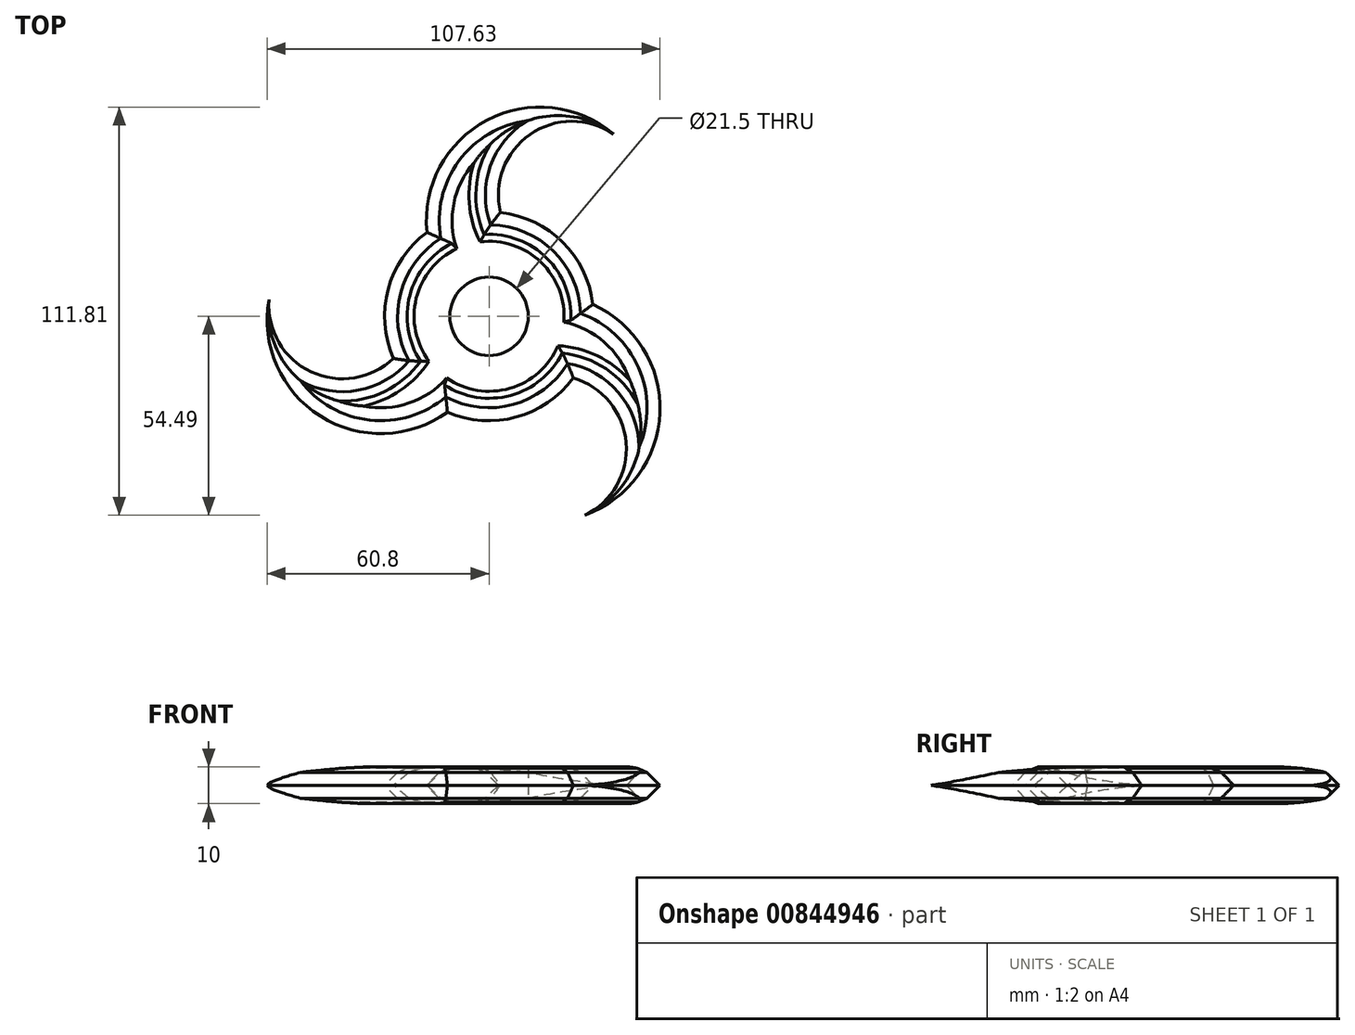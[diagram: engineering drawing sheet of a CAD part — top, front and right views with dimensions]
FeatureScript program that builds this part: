
annotation { "Feature Type Name" : "Feature", "Feature Type Description" : "" }
export const myFeature = defineFeature(function(context is Context, id is Id, definition is map)
    precondition{}
    {
        {
            var Q0;
            Q0=qCreatedBy(makeId("Top.planeOp"),FACE);
            var sketch = newSketch(context, id + "F0", { "sketchPlane" : qUnion([Q0])});
            skCircle(sketch, "E0", {"center": v(0, 0) * mm, "radius": 10.75 * mm});
            skCircle(sketch, "E1", {"center": v(0, 0) * mm, "radius": 28.6 * mm});
            skArc(sketch, "E2", {"start": v(34.08, 49.96) * mm, "mid": v(11.21, 49.81) * mm, "end": v(3.12, 28.43) * mm});
            skArc(sketch, "E3", {"start": v(34.08, 49.96) * mm, "mid": v(-0.57, 53.71) * mm, "end": v(-17.02, 22.99) * mm});
            skArc(sketch, "E4.1.0", {"start": v(-60.3, 4.53) * mm, "mid": v(-46.23, -27.35) * mm, "end": v(-11.4, -26.23) * mm});
            skArc(sketch, "E4.1.1", {"start": v(-60.3, 4.53) * mm, "mid": v(-48.75, -15.2) * mm, "end": v(-26.18, -11.52) * mm});
            skArc(sketch, "E4.2.0", {"start": v(26.23, -54.49) * mm, "mid": v(46.8, -26.36) * mm, "end": v(28.42, 3.24) * mm});
            skArc(sketch, "E4.2.1", {"start": v(26.23, -54.49) * mm, "mid": v(37.53, -34.62) * mm, "end": v(23.06, -16.92) * mm});
            skSolve(sketch);
        }
        {
            var Q0;
            Q0=makeQuery(id+"F0.imprint","IMPRINT",FACE,{"disambiguationData":[TD([[makeQuery(id+"F0.imprint","IMPRINT",EDGE,{"derivedFrom":sQuery(id+"F0.wireOp",EDGE,"E0")}),-1.0]])]});
            extrude(context, id + "F1", {"entities" : qUnion([Q0]), "depth" : 10 * mm, "offsetDistance" : 25 * mm});
        }
        {
            var Q0;
            {var subQ0=sQuery(id+"F0.wireOp",EDGE,"E2");Q0=makeQuery(id+"F0.imprint","IMPRINT",FACE,{"disambiguationData":[TD([[makeQuery(id+"F0.imprint","IMPRINT",EDGE,{"derivedFrom":subQ0}),-1.0]])]});}
            var Q1;
            {var subQ0=sQuery(id+"F0.wireOp",EDGE,"E4.1.0");Q1=makeQuery(id+"F0.imprint","IMPRINT",FACE,{"disambiguationData":[TD([[makeQuery(id+"F0.imprint","IMPRINT",EDGE,{"derivedFrom":subQ0}),1.0]])]});}
            var Q2;
            {var subQ0=sQuery(id+"F0.wireOp",EDGE,"E4.2.0");Q2=makeQuery(id+"F0.imprint","IMPRINT",FACE,{"disambiguationData":[TD([[makeQuery(id+"F0.imprint","IMPRINT",EDGE,{"derivedFrom":subQ0}),1.0]])]});}
            var Q3;
            {var subQ0=sQuery(id+"F0.wireOp",EDGE,"E4.3.0");Q3=makeQuery(id+"F0.imprint","IMPRINT",FACE,{"disambiguationData":[TD([[makeQuery(id+"F0.imprint","IMPRINT",EDGE,{"derivedFrom":subQ0}),1.0]])]});}
            var Q4;
            {var subQ0=sQuery(id+"F0.wireOp",EDGE,"E4.4.0");Q4=makeQuery(id+"F0.imprint","IMPRINT",FACE,{"disambiguationData":[TD([[makeQuery(id+"F0.imprint","IMPRINT",EDGE,{"derivedFrom":subQ0}),1.0]])]});}
            extrude(context, id + "F2", {"entities" : qUnion([Q0, Q1, Q2, Q3, Q4]), "operationType" : NewBodyOperationType.ADD, "depth" : 10 * mm, "offsetDistance" : 25 * mm});
        }
        {
            var Q0;
            Q0=makeQuery(id+"F2.opExtrude","CAP_EDGE",EDGE,{"disambiguationData":[OSD([sQuery(id+"F0.wireOp",EDGE,"E4.1.1")])],"isStart":false});
            var Q1;
            Q1=makeQuery(id+"F2.opExtrude","CAP_EDGE",EDGE,{"disambiguationData":[OSD([sQuery(id+"F0.wireOp",EDGE,"E2")])],"isStart":false});
            var Q2;
            Q2=makeQuery(id+"F2.opExtrude","CAP_EDGE",EDGE,{"disambiguationData":[OSD([sQuery(id+"F0.wireOp",EDGE,"E4.4.1")])],"isStart":false});
            var Q3;
            Q3=makeQuery(id+"F2.opExtrude","CAP_EDGE",EDGE,{"disambiguationData":[OSD([sQuery(id+"F0.wireOp",EDGE,"E4.3.1")])],"isStart":false});
            var Q4;
            Q4=makeQuery(id+"F2.opExtrude","CAP_EDGE",EDGE,{"disambiguationData":[OSD([sQuery(id+"F0.wireOp",EDGE,"E4.2.1")])],"isStart":false});
            var Q5;
            Q5=makeQuery(id+"F2.opExtrude","CAP_EDGE",EDGE,{"disambiguationData":[OSD([sQuery(id+"F0.wireOp",EDGE,"E3")])],"isStart":false});
            var Q6;
            Q6=makeQuery(id+"F2.opExtrude","CAP_EDGE",EDGE,{"disambiguationData":[OSD([sQuery(id+"F0.wireOp",EDGE,"E4.4.0")])],"isStart":false});
            var Q7;
            Q7=makeQuery(id+"F2.opExtrude","CAP_EDGE",EDGE,{"disambiguationData":[OSD([sQuery(id+"F0.wireOp",EDGE,"E4.3.0")])],"isStart":false});
            var Q8;
            Q8=makeQuery(id+"F2.opExtrude","CAP_EDGE",EDGE,{"disambiguationData":[OSD([sQuery(id+"F0.wireOp",EDGE,"E4.2.0")])],"isStart":false});
            var Q9;
            Q9=makeQuery(id+"F2.opExtrude","CAP_EDGE",EDGE,{"disambiguationData":[OSD([sQuery(id+"F0.wireOp",EDGE,"E4.1.0")])],"isStart":false});
            chamfer(context, id + "F3", {"entities" : qUnion([Q0, Q1, Q2, Q3, Q4, Q5, Q6, Q7, Q8, Q9]), "width" : 5 * mm, "tangentPropagation" : true});
        }
        {
            var Q0;
            {var subQ0=sQuery(id+"F0.wireOp",EDGE,"E3");var subQ1=sQuery(id+"F0.wireOp",EDGE,"E1");Q0=makeQuery(id+"F2.boolean.opBoolean","SPLIT",EDGE,{"disambiguationData":[TD([makeQuery(id+"F2.opExtrude","SWEPT_FACE",FACE,{"disambiguationData":[OSD([subQ0])]})])],"derivedFrom":makeQuery(id+"F1.opExtrude","CAP_EDGE",EDGE,{"disambiguationData":[OSD([subQ1])],"isStart":false})});}
            var Q1;
            {var subQ0=sQuery(id+"F0.wireOp",EDGE,"E2");var subQ1=sQuery(id+"F0.wireOp",EDGE,"E1");Q1=makeQuery(id+"F2.boolean.opBoolean","SPLIT",EDGE,{"disambiguationData":[TD([makeQuery(id+"F2.opExtrude","SWEPT_FACE",FACE,{"disambiguationData":[OSD([subQ0])]})])],"derivedFrom":makeQuery(id+"F1.opExtrude","CAP_EDGE",EDGE,{"disambiguationData":[OSD([subQ1])],"isStart":false})});}
            var Q2;
            {var subQ0=sQuery(id+"F0.wireOp",EDGE,"E1");var subQ2=sQuery(id+"F0.wireOp",EDGE,"E4.3.0");Q2=makeQuery(id+"F2.boolean.opBoolean","SPLIT",EDGE,{"disambiguationData":[TD([makeQuery(id+"F2.opExtrude","SWEPT_FACE",FACE,{"disambiguationData":[OSD([subQ2])]})])],"derivedFrom":makeQuery(id+"F1.opExtrude","CAP_EDGE",EDGE,{"disambiguationData":[OSD([subQ0])],"isStart":false})});}
            var Q3;
            {var subQ0=sQuery(id+"F0.wireOp",EDGE,"E1");var subQ1=sQuery(id+"F0.wireOp",EDGE,"E4.2.0");Q3=makeQuery(id+"F2.boolean.opBoolean","SPLIT",EDGE,{"disambiguationData":[TD([makeQuery(id+"F2.opExtrude","SWEPT_FACE",FACE,{"disambiguationData":[OSD([subQ1])]})])],"derivedFrom":makeQuery(id+"F1.opExtrude","CAP_EDGE",EDGE,{"disambiguationData":[OSD([subQ0])],"isStart":false})});}
            var Q4;
            {var subQ0=sQuery(id+"F0.wireOp",EDGE,"E1");var subQ2=sQuery(id+"F0.wireOp",EDGE,"E4.1.0");Q4=makeQuery(id+"F2.boolean.opBoolean","SPLIT",EDGE,{"disambiguationData":[TD([makeQuery(id+"F2.opExtrude","SWEPT_FACE",FACE,{"disambiguationData":[OSD([subQ2])]})])],"derivedFrom":makeQuery(id+"F1.opExtrude","CAP_EDGE",EDGE,{"disambiguationData":[OSD([subQ0])],"isStart":false})});}
            chamfer(context, id + "F4", {"entities" : qUnion([Q0, Q1, Q2, Q3, Q4]), "width" : 5 * mm, "tangentPropagation" : true});
        }
        {
            var Q0;
            {var subQ0=sQuery(id+"F0.wireOp",EDGE,"E2");var subQ1=sQuery(id+"F0.wireOp",EDGE,"E1");Q0=makeQuery(id+"F2.boolean.opBoolean","SPLIT",EDGE,{"disambiguationData":[TD([makeQuery(id+"F2.opExtrude","SWEPT_FACE",FACE,{"disambiguationData":[OSD([subQ0])]})])],"derivedFrom":makeQuery(id+"F1.opExtrude","CAP_EDGE",EDGE,{"disambiguationData":[OSD([subQ1])],"isStart":true})});}
            var Q1;
            Q1=makeQuery(id+"F2.opExtrude","CAP_EDGE",EDGE,{"disambiguationData":[OSD([sQuery(id+"F0.wireOp",EDGE,"E4.4.0")])],"isStart":true});
            var Q2;
            Q2=makeQuery(id+"F2.opExtrude","CAP_EDGE",EDGE,{"disambiguationData":[OSD([sQuery(id+"F0.wireOp",EDGE,"E4.4.1")])],"isStart":true});
            var Q3;
            {var subQ0=sQuery(id+"F0.wireOp",EDGE,"E1");var subQ2=sQuery(id+"F0.wireOp",EDGE,"E4.3.0");Q3=makeQuery(id+"F2.boolean.opBoolean","SPLIT",EDGE,{"disambiguationData":[TD([makeQuery(id+"F2.opExtrude","SWEPT_FACE",FACE,{"disambiguationData":[OSD([subQ2])]})])],"derivedFrom":makeQuery(id+"F1.opExtrude","CAP_EDGE",EDGE,{"disambiguationData":[OSD([subQ0])],"isStart":true})});}
            var Q4;
            Q4=makeQuery(id+"F2.opExtrude","CAP_EDGE",EDGE,{"disambiguationData":[OSD([sQuery(id+"F0.wireOp",EDGE,"E4.3.0")])],"isStart":true});
            var Q5;
            Q5=makeQuery(id+"F2.opExtrude","CAP_EDGE",EDGE,{"disambiguationData":[OSD([sQuery(id+"F0.wireOp",EDGE,"E4.3.1")])],"isStart":true});
            var Q6;
            Q6=makeQuery(id+"F2.opExtrude","CAP_EDGE",EDGE,{"disambiguationData":[OSD([sQuery(id+"F0.wireOp",EDGE,"E4.2.0")])],"isStart":true});
            var Q7;
            Q7=makeQuery(id+"F2.opExtrude","CAP_EDGE",EDGE,{"disambiguationData":[OSD([sQuery(id+"F0.wireOp",EDGE,"E4.2.1")])],"isStart":true});
            var Q8;
            Q8=makeQuery(id+"F2.opExtrude","CAP_EDGE",EDGE,{"disambiguationData":[OSD([sQuery(id+"F0.wireOp",EDGE,"E4.1.0")])],"isStart":true});
            var Q9;
            Q9=makeQuery(id+"F2.opExtrude","CAP_EDGE",EDGE,{"disambiguationData":[OSD([sQuery(id+"F0.wireOp",EDGE,"E4.1.1")])],"isStart":true});
            var Q10;
            Q10=makeQuery(id+"F2.opExtrude","CAP_EDGE",EDGE,{"disambiguationData":[OSD([sQuery(id+"F0.wireOp",EDGE,"E2")])],"isStart":true});
            var Q11;
            Q11=makeQuery(id+"F2.opExtrude","CAP_EDGE",EDGE,{"disambiguationData":[OSD([sQuery(id+"F0.wireOp",EDGE,"E3")])],"isStart":true});
            var Q12;
            {var subQ0=sQuery(id+"F0.wireOp",EDGE,"E3");var subQ1=sQuery(id+"F0.wireOp",EDGE,"E1");Q12=makeQuery(id+"F2.boolean.opBoolean","SPLIT",EDGE,{"disambiguationData":[TD([makeQuery(id+"F2.opExtrude","SWEPT_FACE",FACE,{"disambiguationData":[OSD([subQ0])]})])],"derivedFrom":makeQuery(id+"F1.opExtrude","CAP_EDGE",EDGE,{"disambiguationData":[OSD([subQ1])],"isStart":true})});}
            var Q13;
            {var subQ0=sQuery(id+"F0.wireOp",EDGE,"E1");var subQ2=sQuery(id+"F0.wireOp",EDGE,"E4.1.0");Q13=makeQuery(id+"F2.boolean.opBoolean","SPLIT",EDGE,{"disambiguationData":[TD([makeQuery(id+"F2.opExtrude","SWEPT_FACE",FACE,{"disambiguationData":[OSD([subQ2])]})])],"derivedFrom":makeQuery(id+"F1.opExtrude","CAP_EDGE",EDGE,{"disambiguationData":[OSD([subQ0])],"isStart":true})});}
            var Q14;
            {var subQ0=sQuery(id+"F0.wireOp",EDGE,"E1");var subQ1=sQuery(id+"F0.wireOp",EDGE,"E4.2.0");Q14=makeQuery(id+"F2.boolean.opBoolean","SPLIT",EDGE,{"disambiguationData":[TD([makeQuery(id+"F2.opExtrude","SWEPT_FACE",FACE,{"disambiguationData":[OSD([subQ1])]})])],"derivedFrom":makeQuery(id+"F1.opExtrude","CAP_EDGE",EDGE,{"disambiguationData":[OSD([subQ0])],"isStart":true})});}
            chamfer(context, id + "F5", {"entities" : qUnion([Q0, Q1, Q2, Q3, Q4, Q5, Q6, Q7, Q8, Q9, Q10, Q11, Q12, Q13, Q14]), "width" : 5 * mm, "tangentPropagation" : true});
        }
        {
            var Q0;
            {var subQ0=sQuery(id+"F0.wireOp",EDGE,"E1");var subQ1=sQuery(id+"F0.wireOp",EDGE,"E3");Q0=makeQuery(id+"F5.opChamfer","BLEND_EDGE",EDGE,{"blendedFrom":[makeQuery(id+"F2.opExtrude","CAP_EDGE",EDGE,{"disambiguationData":[OSD([subQ1])],"isStart":true}),makeQuery(id+"F2.boolean.opBoolean","MERGE",FACE,{"derivedFrom":[makeQuery(id+"F1.opExtrude","CAP_FACE",FACE,{"disambiguationData":[OSD([sQuery(id+"F0.wireOp",EDGE,"E0"),subQ0])],"isStart":true}),makeQuery(id+"F2.opExtrude","CAP_FACE",FACE,{"disambiguationData":[OSD([subQ0,sQuery(id+"F0.wireOp",EDGE,"E4.4.0"),sQuery(id+"F0.wireOp",EDGE,"E4.4.1")])],"isStart":true}),makeQuery(id+"F2.opExtrude","CAP_FACE",FACE,{"disambiguationData":[OSD([subQ0,sQuery(id+"F0.wireOp",EDGE,"E2"),subQ1])],"isStart":true}),makeQuery(id+"F2.opExtrude","CAP_FACE",FACE,{"disambiguationData":[OSD([subQ0,sQuery(id+"F0.wireOp",EDGE,"E4.1.0"),sQuery(id+"F0.wireOp",EDGE,"E4.1.1")])],"isStart":true}),makeQuery(id+"F2.opExtrude","CAP_FACE",FACE,{"disambiguationData":[OSD([subQ0,sQuery(id+"F0.wireOp",EDGE,"E4.2.0"),sQuery(id+"F0.wireOp",EDGE,"E4.2.1")])],"isStart":true}),makeQuery(id+"F2.opExtrude","CAP_FACE",FACE,{"disambiguationData":[OSD([subQ0,sQuery(id+"F0.wireOp",EDGE,"E4.3.0"),sQuery(id+"F0.wireOp",EDGE,"E4.3.1")])],"isStart":true})]})],"blendedInto":[makeQuery(id+"F2.boolean.opBoolean","MERGE",FACE,{"derivedFrom":[makeQuery(id+"F1.opExtrude","CAP_FACE",FACE,{"disambiguationData":[OSD([sQuery(id+"F0.wireOp",EDGE,"E0"),subQ0])],"isStart":true}),makeQuery(id+"F2.opExtrude","CAP_FACE",FACE,{"disambiguationData":[OSD([subQ0,sQuery(id+"F0.wireOp",EDGE,"E4.4.0"),sQuery(id+"F0.wireOp",EDGE,"E4.4.1")])],"isStart":true}),makeQuery(id+"F2.opExtrude","CAP_FACE",FACE,{"disambiguationData":[OSD([subQ0,sQuery(id+"F0.wireOp",EDGE,"E2"),subQ1])],"isStart":true}),makeQuery(id+"F2.opExtrude","CAP_FACE",FACE,{"disambiguationData":[OSD([subQ0,sQuery(id+"F0.wireOp",EDGE,"E4.1.0"),sQuery(id+"F0.wireOp",EDGE,"E4.1.1")])],"isStart":true}),makeQuery(id+"F2.opExtrude","CAP_FACE",FACE,{"disambiguationData":[OSD([subQ0,sQuery(id+"F0.wireOp",EDGE,"E4.2.0"),sQuery(id+"F0.wireOp",EDGE,"E4.2.1")])],"isStart":true}),makeQuery(id+"F2.opExtrude","CAP_FACE",FACE,{"disambiguationData":[OSD([subQ0,sQuery(id+"F0.wireOp",EDGE,"E4.3.0"),sQuery(id+"F0.wireOp",EDGE,"E4.3.1")])],"isStart":true})]})]});}
            var Q1;
            {var subQ0=sQuery(id+"F0.wireOp",EDGE,"E1");var subQ1=sQuery(id+"F0.wireOp",EDGE,"E2");Q1=makeQuery(id+"F5.opChamfer","BLEND_EDGE",EDGE,{"blendedFrom":[makeQuery(id+"F2.opExtrude","CAP_EDGE",EDGE,{"disambiguationData":[OSD([subQ1])],"isStart":true}),makeQuery(id+"F2.boolean.opBoolean","MERGE",FACE,{"derivedFrom":[makeQuery(id+"F1.opExtrude","CAP_FACE",FACE,{"disambiguationData":[OSD([sQuery(id+"F0.wireOp",EDGE,"E0"),subQ0])],"isStart":true}),makeQuery(id+"F2.opExtrude","CAP_FACE",FACE,{"disambiguationData":[OSD([subQ0,sQuery(id+"F0.wireOp",EDGE,"E4.4.0"),sQuery(id+"F0.wireOp",EDGE,"E4.4.1")])],"isStart":true}),makeQuery(id+"F2.opExtrude","CAP_FACE",FACE,{"disambiguationData":[OSD([subQ0,subQ1,sQuery(id+"F0.wireOp",EDGE,"E3")])],"isStart":true}),makeQuery(id+"F2.opExtrude","CAP_FACE",FACE,{"disambiguationData":[OSD([subQ0,sQuery(id+"F0.wireOp",EDGE,"E4.1.0"),sQuery(id+"F0.wireOp",EDGE,"E4.1.1")])],"isStart":true}),makeQuery(id+"F2.opExtrude","CAP_FACE",FACE,{"disambiguationData":[OSD([subQ0,sQuery(id+"F0.wireOp",EDGE,"E4.2.0"),sQuery(id+"F0.wireOp",EDGE,"E4.2.1")])],"isStart":true}),makeQuery(id+"F2.opExtrude","CAP_FACE",FACE,{"disambiguationData":[OSD([subQ0,sQuery(id+"F0.wireOp",EDGE,"E4.3.0"),sQuery(id+"F0.wireOp",EDGE,"E4.3.1")])],"isStart":true})]})],"blendedInto":[makeQuery(id+"F2.boolean.opBoolean","MERGE",FACE,{"derivedFrom":[makeQuery(id+"F1.opExtrude","CAP_FACE",FACE,{"disambiguationData":[OSD([sQuery(id+"F0.wireOp",EDGE,"E0"),subQ0])],"isStart":true}),makeQuery(id+"F2.opExtrude","CAP_FACE",FACE,{"disambiguationData":[OSD([subQ0,sQuery(id+"F0.wireOp",EDGE,"E4.4.0"),sQuery(id+"F0.wireOp",EDGE,"E4.4.1")])],"isStart":true}),makeQuery(id+"F2.opExtrude","CAP_FACE",FACE,{"disambiguationData":[OSD([subQ0,subQ1,sQuery(id+"F0.wireOp",EDGE,"E3")])],"isStart":true}),makeQuery(id+"F2.opExtrude","CAP_FACE",FACE,{"disambiguationData":[OSD([subQ0,sQuery(id+"F0.wireOp",EDGE,"E4.1.0"),sQuery(id+"F0.wireOp",EDGE,"E4.1.1")])],"isStart":true}),makeQuery(id+"F2.opExtrude","CAP_FACE",FACE,{"disambiguationData":[OSD([subQ0,sQuery(id+"F0.wireOp",EDGE,"E4.2.0"),sQuery(id+"F0.wireOp",EDGE,"E4.2.1")])],"isStart":true}),makeQuery(id+"F2.opExtrude","CAP_FACE",FACE,{"disambiguationData":[OSD([subQ0,sQuery(id+"F0.wireOp",EDGE,"E4.3.0"),sQuery(id+"F0.wireOp",EDGE,"E4.3.1")])],"isStart":true})]})]});}
            var Q2;
            {var subQ0=sQuery(id+"F0.wireOp",EDGE,"E1");var subQ1=sQuery(id+"F0.wireOp",EDGE,"E4.1.1");Q2=makeQuery(id+"F5.opChamfer","BLEND_EDGE",EDGE,{"blendedFrom":[makeQuery(id+"F2.opExtrude","CAP_EDGE",EDGE,{"disambiguationData":[OSD([subQ1])],"isStart":true}),makeQuery(id+"F2.boolean.opBoolean","MERGE",FACE,{"derivedFrom":[makeQuery(id+"F1.opExtrude","CAP_FACE",FACE,{"disambiguationData":[OSD([sQuery(id+"F0.wireOp",EDGE,"E0"),subQ0])],"isStart":true}),makeQuery(id+"F2.opExtrude","CAP_FACE",FACE,{"disambiguationData":[OSD([subQ0,sQuery(id+"F0.wireOp",EDGE,"E4.4.0"),sQuery(id+"F0.wireOp",EDGE,"E4.4.1")])],"isStart":true}),makeQuery(id+"F2.opExtrude","CAP_FACE",FACE,{"disambiguationData":[OSD([subQ0,sQuery(id+"F0.wireOp",EDGE,"E2"),sQuery(id+"F0.wireOp",EDGE,"E3")])],"isStart":true}),makeQuery(id+"F2.opExtrude","CAP_FACE",FACE,{"disambiguationData":[OSD([subQ0,sQuery(id+"F0.wireOp",EDGE,"E4.1.0"),subQ1])],"isStart":true}),makeQuery(id+"F2.opExtrude","CAP_FACE",FACE,{"disambiguationData":[OSD([subQ0,sQuery(id+"F0.wireOp",EDGE,"E4.2.0"),sQuery(id+"F0.wireOp",EDGE,"E4.2.1")])],"isStart":true}),makeQuery(id+"F2.opExtrude","CAP_FACE",FACE,{"disambiguationData":[OSD([subQ0,sQuery(id+"F0.wireOp",EDGE,"E4.3.0"),sQuery(id+"F0.wireOp",EDGE,"E4.3.1")])],"isStart":true})]})],"blendedInto":[makeQuery(id+"F2.boolean.opBoolean","MERGE",FACE,{"derivedFrom":[makeQuery(id+"F1.opExtrude","CAP_FACE",FACE,{"disambiguationData":[OSD([sQuery(id+"F0.wireOp",EDGE,"E0"),subQ0])],"isStart":true}),makeQuery(id+"F2.opExtrude","CAP_FACE",FACE,{"disambiguationData":[OSD([subQ0,sQuery(id+"F0.wireOp",EDGE,"E4.4.0"),sQuery(id+"F0.wireOp",EDGE,"E4.4.1")])],"isStart":true}),makeQuery(id+"F2.opExtrude","CAP_FACE",FACE,{"disambiguationData":[OSD([subQ0,sQuery(id+"F0.wireOp",EDGE,"E2"),sQuery(id+"F0.wireOp",EDGE,"E3")])],"isStart":true}),makeQuery(id+"F2.opExtrude","CAP_FACE",FACE,{"disambiguationData":[OSD([subQ0,sQuery(id+"F0.wireOp",EDGE,"E4.1.0"),subQ1])],"isStart":true}),makeQuery(id+"F2.opExtrude","CAP_FACE",FACE,{"disambiguationData":[OSD([subQ0,sQuery(id+"F0.wireOp",EDGE,"E4.2.0"),sQuery(id+"F0.wireOp",EDGE,"E4.2.1")])],"isStart":true}),makeQuery(id+"F2.opExtrude","CAP_FACE",FACE,{"disambiguationData":[OSD([subQ0,sQuery(id+"F0.wireOp",EDGE,"E4.3.0"),sQuery(id+"F0.wireOp",EDGE,"E4.3.1")])],"isStart":true})]})]});}
            var Q3;
            {var subQ0=sQuery(id+"F0.wireOp",EDGE,"E1");var subQ1=sQuery(id+"F0.wireOp",EDGE,"E4.1.0");Q3=makeQuery(id+"F5.opChamfer","BLEND_EDGE",EDGE,{"blendedFrom":[makeQuery(id+"F2.opExtrude","CAP_EDGE",EDGE,{"disambiguationData":[OSD([subQ1])],"isStart":true}),makeQuery(id+"F2.boolean.opBoolean","MERGE",FACE,{"derivedFrom":[makeQuery(id+"F1.opExtrude","CAP_FACE",FACE,{"disambiguationData":[OSD([sQuery(id+"F0.wireOp",EDGE,"E0"),subQ0])],"isStart":true}),makeQuery(id+"F2.opExtrude","CAP_FACE",FACE,{"disambiguationData":[OSD([subQ0,sQuery(id+"F0.wireOp",EDGE,"E4.4.0"),sQuery(id+"F0.wireOp",EDGE,"E4.4.1")])],"isStart":true}),makeQuery(id+"F2.opExtrude","CAP_FACE",FACE,{"disambiguationData":[OSD([subQ0,sQuery(id+"F0.wireOp",EDGE,"E2"),sQuery(id+"F0.wireOp",EDGE,"E3")])],"isStart":true}),makeQuery(id+"F2.opExtrude","CAP_FACE",FACE,{"disambiguationData":[OSD([subQ0,subQ1,sQuery(id+"F0.wireOp",EDGE,"E4.1.1")])],"isStart":true}),makeQuery(id+"F2.opExtrude","CAP_FACE",FACE,{"disambiguationData":[OSD([subQ0,sQuery(id+"F0.wireOp",EDGE,"E4.2.0"),sQuery(id+"F0.wireOp",EDGE,"E4.2.1")])],"isStart":true}),makeQuery(id+"F2.opExtrude","CAP_FACE",FACE,{"disambiguationData":[OSD([subQ0,sQuery(id+"F0.wireOp",EDGE,"E4.3.0"),sQuery(id+"F0.wireOp",EDGE,"E4.3.1")])],"isStart":true})]})],"blendedInto":[makeQuery(id+"F2.boolean.opBoolean","MERGE",FACE,{"derivedFrom":[makeQuery(id+"F1.opExtrude","CAP_FACE",FACE,{"disambiguationData":[OSD([sQuery(id+"F0.wireOp",EDGE,"E0"),subQ0])],"isStart":true}),makeQuery(id+"F2.opExtrude","CAP_FACE",FACE,{"disambiguationData":[OSD([subQ0,sQuery(id+"F0.wireOp",EDGE,"E4.4.0"),sQuery(id+"F0.wireOp",EDGE,"E4.4.1")])],"isStart":true}),makeQuery(id+"F2.opExtrude","CAP_FACE",FACE,{"disambiguationData":[OSD([subQ0,sQuery(id+"F0.wireOp",EDGE,"E2"),sQuery(id+"F0.wireOp",EDGE,"E3")])],"isStart":true}),makeQuery(id+"F2.opExtrude","CAP_FACE",FACE,{"disambiguationData":[OSD([subQ0,subQ1,sQuery(id+"F0.wireOp",EDGE,"E4.1.1")])],"isStart":true}),makeQuery(id+"F2.opExtrude","CAP_FACE",FACE,{"disambiguationData":[OSD([subQ0,sQuery(id+"F0.wireOp",EDGE,"E4.2.0"),sQuery(id+"F0.wireOp",EDGE,"E4.2.1")])],"isStart":true}),makeQuery(id+"F2.opExtrude","CAP_FACE",FACE,{"disambiguationData":[OSD([subQ0,sQuery(id+"F0.wireOp",EDGE,"E4.3.0"),sQuery(id+"F0.wireOp",EDGE,"E4.3.1")])],"isStart":true})]})]});}
            var Q4;
            {var subQ0=sQuery(id+"F0.wireOp",EDGE,"E1");var subQ1=sQuery(id+"F0.wireOp",EDGE,"E4.2.1");Q4=makeQuery(id+"F5.opChamfer","BLEND_EDGE",EDGE,{"blendedFrom":[makeQuery(id+"F2.opExtrude","CAP_EDGE",EDGE,{"disambiguationData":[OSD([subQ1])],"isStart":true}),makeQuery(id+"F2.boolean.opBoolean","MERGE",FACE,{"derivedFrom":[makeQuery(id+"F1.opExtrude","CAP_FACE",FACE,{"disambiguationData":[OSD([sQuery(id+"F0.wireOp",EDGE,"E0"),subQ0])],"isStart":true}),makeQuery(id+"F2.opExtrude","CAP_FACE",FACE,{"disambiguationData":[OSD([subQ0,sQuery(id+"F0.wireOp",EDGE,"E4.4.0"),sQuery(id+"F0.wireOp",EDGE,"E4.4.1")])],"isStart":true}),makeQuery(id+"F2.opExtrude","CAP_FACE",FACE,{"disambiguationData":[OSD([subQ0,sQuery(id+"F0.wireOp",EDGE,"E2"),sQuery(id+"F0.wireOp",EDGE,"E3")])],"isStart":true}),makeQuery(id+"F2.opExtrude","CAP_FACE",FACE,{"disambiguationData":[OSD([subQ0,sQuery(id+"F0.wireOp",EDGE,"E4.1.0"),sQuery(id+"F0.wireOp",EDGE,"E4.1.1")])],"isStart":true}),makeQuery(id+"F2.opExtrude","CAP_FACE",FACE,{"disambiguationData":[OSD([subQ0,sQuery(id+"F0.wireOp",EDGE,"E4.2.0"),subQ1])],"isStart":true}),makeQuery(id+"F2.opExtrude","CAP_FACE",FACE,{"disambiguationData":[OSD([subQ0,sQuery(id+"F0.wireOp",EDGE,"E4.3.0"),sQuery(id+"F0.wireOp",EDGE,"E4.3.1")])],"isStart":true})]})],"blendedInto":[makeQuery(id+"F2.boolean.opBoolean","MERGE",FACE,{"derivedFrom":[makeQuery(id+"F1.opExtrude","CAP_FACE",FACE,{"disambiguationData":[OSD([sQuery(id+"F0.wireOp",EDGE,"E0"),subQ0])],"isStart":true}),makeQuery(id+"F2.opExtrude","CAP_FACE",FACE,{"disambiguationData":[OSD([subQ0,sQuery(id+"F0.wireOp",EDGE,"E4.4.0"),sQuery(id+"F0.wireOp",EDGE,"E4.4.1")])],"isStart":true}),makeQuery(id+"F2.opExtrude","CAP_FACE",FACE,{"disambiguationData":[OSD([subQ0,sQuery(id+"F0.wireOp",EDGE,"E2"),sQuery(id+"F0.wireOp",EDGE,"E3")])],"isStart":true}),makeQuery(id+"F2.opExtrude","CAP_FACE",FACE,{"disambiguationData":[OSD([subQ0,sQuery(id+"F0.wireOp",EDGE,"E4.1.0"),sQuery(id+"F0.wireOp",EDGE,"E4.1.1")])],"isStart":true}),makeQuery(id+"F2.opExtrude","CAP_FACE",FACE,{"disambiguationData":[OSD([subQ0,sQuery(id+"F0.wireOp",EDGE,"E4.2.0"),subQ1])],"isStart":true}),makeQuery(id+"F2.opExtrude","CAP_FACE",FACE,{"disambiguationData":[OSD([subQ0,sQuery(id+"F0.wireOp",EDGE,"E4.3.0"),sQuery(id+"F0.wireOp",EDGE,"E4.3.1")])],"isStart":true})]})]});}
            var Q5;
            {var subQ0=sQuery(id+"F0.wireOp",EDGE,"E1");var subQ1=sQuery(id+"F0.wireOp",EDGE,"E4.2.0");Q5=makeQuery(id+"F5.opChamfer","BLEND_EDGE",EDGE,{"blendedFrom":[makeQuery(id+"F2.opExtrude","CAP_EDGE",EDGE,{"disambiguationData":[OSD([subQ1])],"isStart":true}),makeQuery(id+"F2.boolean.opBoolean","MERGE",FACE,{"derivedFrom":[makeQuery(id+"F1.opExtrude","CAP_FACE",FACE,{"disambiguationData":[OSD([sQuery(id+"F0.wireOp",EDGE,"E0"),subQ0])],"isStart":true}),makeQuery(id+"F2.opExtrude","CAP_FACE",FACE,{"disambiguationData":[OSD([subQ0,sQuery(id+"F0.wireOp",EDGE,"E4.4.0"),sQuery(id+"F0.wireOp",EDGE,"E4.4.1")])],"isStart":true}),makeQuery(id+"F2.opExtrude","CAP_FACE",FACE,{"disambiguationData":[OSD([subQ0,sQuery(id+"F0.wireOp",EDGE,"E2"),sQuery(id+"F0.wireOp",EDGE,"E3")])],"isStart":true}),makeQuery(id+"F2.opExtrude","CAP_FACE",FACE,{"disambiguationData":[OSD([subQ0,sQuery(id+"F0.wireOp",EDGE,"E4.1.0"),sQuery(id+"F0.wireOp",EDGE,"E4.1.1")])],"isStart":true}),makeQuery(id+"F2.opExtrude","CAP_FACE",FACE,{"disambiguationData":[OSD([subQ0,subQ1,sQuery(id+"F0.wireOp",EDGE,"E4.2.1")])],"isStart":true}),makeQuery(id+"F2.opExtrude","CAP_FACE",FACE,{"disambiguationData":[OSD([subQ0,sQuery(id+"F0.wireOp",EDGE,"E4.3.0"),sQuery(id+"F0.wireOp",EDGE,"E4.3.1")])],"isStart":true})]})],"blendedInto":[makeQuery(id+"F2.boolean.opBoolean","MERGE",FACE,{"derivedFrom":[makeQuery(id+"F1.opExtrude","CAP_FACE",FACE,{"disambiguationData":[OSD([sQuery(id+"F0.wireOp",EDGE,"E0"),subQ0])],"isStart":true}),makeQuery(id+"F2.opExtrude","CAP_FACE",FACE,{"disambiguationData":[OSD([subQ0,sQuery(id+"F0.wireOp",EDGE,"E4.4.0"),sQuery(id+"F0.wireOp",EDGE,"E4.4.1")])],"isStart":true}),makeQuery(id+"F2.opExtrude","CAP_FACE",FACE,{"disambiguationData":[OSD([subQ0,sQuery(id+"F0.wireOp",EDGE,"E2"),sQuery(id+"F0.wireOp",EDGE,"E3")])],"isStart":true}),makeQuery(id+"F2.opExtrude","CAP_FACE",FACE,{"disambiguationData":[OSD([subQ0,sQuery(id+"F0.wireOp",EDGE,"E4.1.0"),sQuery(id+"F0.wireOp",EDGE,"E4.1.1")])],"isStart":true}),makeQuery(id+"F2.opExtrude","CAP_FACE",FACE,{"disambiguationData":[OSD([subQ0,subQ1,sQuery(id+"F0.wireOp",EDGE,"E4.2.1")])],"isStart":true}),makeQuery(id+"F2.opExtrude","CAP_FACE",FACE,{"disambiguationData":[OSD([subQ0,sQuery(id+"F0.wireOp",EDGE,"E4.3.0"),sQuery(id+"F0.wireOp",EDGE,"E4.3.1")])],"isStart":true})]})]});}
            var Q6;
            {var subQ0=sQuery(id+"F0.wireOp",EDGE,"E4.3.1");var subQ1=sQuery(id+"F0.wireOp",EDGE,"E1");Q6=makeQuery(id+"F5.opChamfer","BLEND_EDGE",EDGE,{"blendedFrom":[makeQuery(id+"F2.opExtrude","CAP_EDGE",EDGE,{"disambiguationData":[OSD([subQ0])],"isStart":true}),makeQuery(id+"F2.boolean.opBoolean","MERGE",FACE,{"derivedFrom":[makeQuery(id+"F1.opExtrude","CAP_FACE",FACE,{"disambiguationData":[OSD([sQuery(id+"F0.wireOp",EDGE,"E0"),subQ1])],"isStart":true}),makeQuery(id+"F2.opExtrude","CAP_FACE",FACE,{"disambiguationData":[OSD([subQ1,sQuery(id+"F0.wireOp",EDGE,"E4.4.0"),sQuery(id+"F0.wireOp",EDGE,"E4.4.1")])],"isStart":true}),makeQuery(id+"F2.opExtrude","CAP_FACE",FACE,{"disambiguationData":[OSD([subQ1,sQuery(id+"F0.wireOp",EDGE,"E2"),sQuery(id+"F0.wireOp",EDGE,"E3")])],"isStart":true}),makeQuery(id+"F2.opExtrude","CAP_FACE",FACE,{"disambiguationData":[OSD([subQ1,sQuery(id+"F0.wireOp",EDGE,"E4.1.0"),sQuery(id+"F0.wireOp",EDGE,"E4.1.1")])],"isStart":true}),makeQuery(id+"F2.opExtrude","CAP_FACE",FACE,{"disambiguationData":[OSD([subQ1,sQuery(id+"F0.wireOp",EDGE,"E4.2.0"),sQuery(id+"F0.wireOp",EDGE,"E4.2.1")])],"isStart":true}),makeQuery(id+"F2.opExtrude","CAP_FACE",FACE,{"disambiguationData":[OSD([subQ1,sQuery(id+"F0.wireOp",EDGE,"E4.3.0"),subQ0])],"isStart":true})]})],"blendedInto":[makeQuery(id+"F2.boolean.opBoolean","MERGE",FACE,{"derivedFrom":[makeQuery(id+"F1.opExtrude","CAP_FACE",FACE,{"disambiguationData":[OSD([sQuery(id+"F0.wireOp",EDGE,"E0"),subQ1])],"isStart":true}),makeQuery(id+"F2.opExtrude","CAP_FACE",FACE,{"disambiguationData":[OSD([subQ1,sQuery(id+"F0.wireOp",EDGE,"E4.4.0"),sQuery(id+"F0.wireOp",EDGE,"E4.4.1")])],"isStart":true}),makeQuery(id+"F2.opExtrude","CAP_FACE",FACE,{"disambiguationData":[OSD([subQ1,sQuery(id+"F0.wireOp",EDGE,"E2"),sQuery(id+"F0.wireOp",EDGE,"E3")])],"isStart":true}),makeQuery(id+"F2.opExtrude","CAP_FACE",FACE,{"disambiguationData":[OSD([subQ1,sQuery(id+"F0.wireOp",EDGE,"E4.1.0"),sQuery(id+"F0.wireOp",EDGE,"E4.1.1")])],"isStart":true}),makeQuery(id+"F2.opExtrude","CAP_FACE",FACE,{"disambiguationData":[OSD([subQ1,sQuery(id+"F0.wireOp",EDGE,"E4.2.0"),sQuery(id+"F0.wireOp",EDGE,"E4.2.1")])],"isStart":true}),makeQuery(id+"F2.opExtrude","CAP_FACE",FACE,{"disambiguationData":[OSD([subQ1,sQuery(id+"F0.wireOp",EDGE,"E4.3.0"),subQ0])],"isStart":true})]})]});}
            var Q7;
            {var subQ0=sQuery(id+"F0.wireOp",EDGE,"E4.3.0");var subQ1=sQuery(id+"F0.wireOp",EDGE,"E1");Q7=makeQuery(id+"F5.opChamfer","BLEND_EDGE",EDGE,{"blendedFrom":[makeQuery(id+"F2.opExtrude","CAP_EDGE",EDGE,{"disambiguationData":[OSD([subQ0])],"isStart":true}),makeQuery(id+"F2.boolean.opBoolean","MERGE",FACE,{"derivedFrom":[makeQuery(id+"F1.opExtrude","CAP_FACE",FACE,{"disambiguationData":[OSD([sQuery(id+"F0.wireOp",EDGE,"E0"),subQ1])],"isStart":true}),makeQuery(id+"F2.opExtrude","CAP_FACE",FACE,{"disambiguationData":[OSD([subQ1,sQuery(id+"F0.wireOp",EDGE,"E4.4.0"),sQuery(id+"F0.wireOp",EDGE,"E4.4.1")])],"isStart":true}),makeQuery(id+"F2.opExtrude","CAP_FACE",FACE,{"disambiguationData":[OSD([subQ1,sQuery(id+"F0.wireOp",EDGE,"E2"),sQuery(id+"F0.wireOp",EDGE,"E3")])],"isStart":true}),makeQuery(id+"F2.opExtrude","CAP_FACE",FACE,{"disambiguationData":[OSD([subQ1,sQuery(id+"F0.wireOp",EDGE,"E4.1.0"),sQuery(id+"F0.wireOp",EDGE,"E4.1.1")])],"isStart":true}),makeQuery(id+"F2.opExtrude","CAP_FACE",FACE,{"disambiguationData":[OSD([subQ1,sQuery(id+"F0.wireOp",EDGE,"E4.2.0"),sQuery(id+"F0.wireOp",EDGE,"E4.2.1")])],"isStart":true}),makeQuery(id+"F2.opExtrude","CAP_FACE",FACE,{"disambiguationData":[OSD([subQ1,subQ0,sQuery(id+"F0.wireOp",EDGE,"E4.3.1")])],"isStart":true})]})],"blendedInto":[makeQuery(id+"F2.boolean.opBoolean","MERGE",FACE,{"derivedFrom":[makeQuery(id+"F1.opExtrude","CAP_FACE",FACE,{"disambiguationData":[OSD([sQuery(id+"F0.wireOp",EDGE,"E0"),subQ1])],"isStart":true}),makeQuery(id+"F2.opExtrude","CAP_FACE",FACE,{"disambiguationData":[OSD([subQ1,sQuery(id+"F0.wireOp",EDGE,"E4.4.0"),sQuery(id+"F0.wireOp",EDGE,"E4.4.1")])],"isStart":true}),makeQuery(id+"F2.opExtrude","CAP_FACE",FACE,{"disambiguationData":[OSD([subQ1,sQuery(id+"F0.wireOp",EDGE,"E2"),sQuery(id+"F0.wireOp",EDGE,"E3")])],"isStart":true}),makeQuery(id+"F2.opExtrude","CAP_FACE",FACE,{"disambiguationData":[OSD([subQ1,sQuery(id+"F0.wireOp",EDGE,"E4.1.0"),sQuery(id+"F0.wireOp",EDGE,"E4.1.1")])],"isStart":true}),makeQuery(id+"F2.opExtrude","CAP_FACE",FACE,{"disambiguationData":[OSD([subQ1,sQuery(id+"F0.wireOp",EDGE,"E4.2.0"),sQuery(id+"F0.wireOp",EDGE,"E4.2.1")])],"isStart":true}),makeQuery(id+"F2.opExtrude","CAP_FACE",FACE,{"disambiguationData":[OSD([subQ1,subQ0,sQuery(id+"F0.wireOp",EDGE,"E4.3.1")])],"isStart":true})]})]});}
            var Q8;
            {var subQ0=sQuery(id+"F0.wireOp",EDGE,"E1");var subQ1=sQuery(id+"F0.wireOp",EDGE,"E4.4.1");Q8=makeQuery(id+"F5.opChamfer","BLEND_EDGE",EDGE,{"blendedFrom":[makeQuery(id+"F2.opExtrude","CAP_EDGE",EDGE,{"disambiguationData":[OSD([subQ1])],"isStart":true}),makeQuery(id+"F2.boolean.opBoolean","MERGE",FACE,{"derivedFrom":[makeQuery(id+"F1.opExtrude","CAP_FACE",FACE,{"disambiguationData":[OSD([sQuery(id+"F0.wireOp",EDGE,"E0"),subQ0])],"isStart":true}),makeQuery(id+"F2.opExtrude","CAP_FACE",FACE,{"disambiguationData":[OSD([subQ0,sQuery(id+"F0.wireOp",EDGE,"E4.4.0"),subQ1])],"isStart":true}),makeQuery(id+"F2.opExtrude","CAP_FACE",FACE,{"disambiguationData":[OSD([subQ0,sQuery(id+"F0.wireOp",EDGE,"E2"),sQuery(id+"F0.wireOp",EDGE,"E3")])],"isStart":true}),makeQuery(id+"F2.opExtrude","CAP_FACE",FACE,{"disambiguationData":[OSD([subQ0,sQuery(id+"F0.wireOp",EDGE,"E4.1.0"),sQuery(id+"F0.wireOp",EDGE,"E4.1.1")])],"isStart":true}),makeQuery(id+"F2.opExtrude","CAP_FACE",FACE,{"disambiguationData":[OSD([subQ0,sQuery(id+"F0.wireOp",EDGE,"E4.2.0"),sQuery(id+"F0.wireOp",EDGE,"E4.2.1")])],"isStart":true}),makeQuery(id+"F2.opExtrude","CAP_FACE",FACE,{"disambiguationData":[OSD([subQ0,sQuery(id+"F0.wireOp",EDGE,"E4.3.0"),sQuery(id+"F0.wireOp",EDGE,"E4.3.1")])],"isStart":true})]})],"blendedInto":[makeQuery(id+"F2.boolean.opBoolean","MERGE",FACE,{"derivedFrom":[makeQuery(id+"F1.opExtrude","CAP_FACE",FACE,{"disambiguationData":[OSD([sQuery(id+"F0.wireOp",EDGE,"E0"),subQ0])],"isStart":true}),makeQuery(id+"F2.opExtrude","CAP_FACE",FACE,{"disambiguationData":[OSD([subQ0,sQuery(id+"F0.wireOp",EDGE,"E4.4.0"),subQ1])],"isStart":true}),makeQuery(id+"F2.opExtrude","CAP_FACE",FACE,{"disambiguationData":[OSD([subQ0,sQuery(id+"F0.wireOp",EDGE,"E2"),sQuery(id+"F0.wireOp",EDGE,"E3")])],"isStart":true}),makeQuery(id+"F2.opExtrude","CAP_FACE",FACE,{"disambiguationData":[OSD([subQ0,sQuery(id+"F0.wireOp",EDGE,"E4.1.0"),sQuery(id+"F0.wireOp",EDGE,"E4.1.1")])],"isStart":true}),makeQuery(id+"F2.opExtrude","CAP_FACE",FACE,{"disambiguationData":[OSD([subQ0,sQuery(id+"F0.wireOp",EDGE,"E4.2.0"),sQuery(id+"F0.wireOp",EDGE,"E4.2.1")])],"isStart":true}),makeQuery(id+"F2.opExtrude","CAP_FACE",FACE,{"disambiguationData":[OSD([subQ0,sQuery(id+"F0.wireOp",EDGE,"E4.3.0"),sQuery(id+"F0.wireOp",EDGE,"E4.3.1")])],"isStart":true})]})]});}
            var Q9;
            {var subQ0=sQuery(id+"F0.wireOp",EDGE,"E1");var subQ1=sQuery(id+"F0.wireOp",EDGE,"E4.4.0");Q9=makeQuery(id+"F5.opChamfer","BLEND_EDGE",EDGE,{"blendedFrom":[makeQuery(id+"F2.opExtrude","CAP_EDGE",EDGE,{"disambiguationData":[OSD([subQ1])],"isStart":true}),makeQuery(id+"F2.boolean.opBoolean","MERGE",FACE,{"derivedFrom":[makeQuery(id+"F1.opExtrude","CAP_FACE",FACE,{"disambiguationData":[OSD([sQuery(id+"F0.wireOp",EDGE,"E0"),subQ0])],"isStart":true}),makeQuery(id+"F2.opExtrude","CAP_FACE",FACE,{"disambiguationData":[OSD([subQ0,subQ1,sQuery(id+"F0.wireOp",EDGE,"E4.4.1")])],"isStart":true}),makeQuery(id+"F2.opExtrude","CAP_FACE",FACE,{"disambiguationData":[OSD([subQ0,sQuery(id+"F0.wireOp",EDGE,"E2"),sQuery(id+"F0.wireOp",EDGE,"E3")])],"isStart":true}),makeQuery(id+"F2.opExtrude","CAP_FACE",FACE,{"disambiguationData":[OSD([subQ0,sQuery(id+"F0.wireOp",EDGE,"E4.1.0"),sQuery(id+"F0.wireOp",EDGE,"E4.1.1")])],"isStart":true}),makeQuery(id+"F2.opExtrude","CAP_FACE",FACE,{"disambiguationData":[OSD([subQ0,sQuery(id+"F0.wireOp",EDGE,"E4.2.0"),sQuery(id+"F0.wireOp",EDGE,"E4.2.1")])],"isStart":true}),makeQuery(id+"F2.opExtrude","CAP_FACE",FACE,{"disambiguationData":[OSD([subQ0,sQuery(id+"F0.wireOp",EDGE,"E4.3.0"),sQuery(id+"F0.wireOp",EDGE,"E4.3.1")])],"isStart":true})]})],"blendedInto":[makeQuery(id+"F2.boolean.opBoolean","MERGE",FACE,{"derivedFrom":[makeQuery(id+"F1.opExtrude","CAP_FACE",FACE,{"disambiguationData":[OSD([sQuery(id+"F0.wireOp",EDGE,"E0"),subQ0])],"isStart":true}),makeQuery(id+"F2.opExtrude","CAP_FACE",FACE,{"disambiguationData":[OSD([subQ0,subQ1,sQuery(id+"F0.wireOp",EDGE,"E4.4.1")])],"isStart":true}),makeQuery(id+"F2.opExtrude","CAP_FACE",FACE,{"disambiguationData":[OSD([subQ0,sQuery(id+"F0.wireOp",EDGE,"E2"),sQuery(id+"F0.wireOp",EDGE,"E3")])],"isStart":true}),makeQuery(id+"F2.opExtrude","CAP_FACE",FACE,{"disambiguationData":[OSD([subQ0,sQuery(id+"F0.wireOp",EDGE,"E4.1.0"),sQuery(id+"F0.wireOp",EDGE,"E4.1.1")])],"isStart":true}),makeQuery(id+"F2.opExtrude","CAP_FACE",FACE,{"disambiguationData":[OSD([subQ0,sQuery(id+"F0.wireOp",EDGE,"E4.2.0"),sQuery(id+"F0.wireOp",EDGE,"E4.2.1")])],"isStart":true}),makeQuery(id+"F2.opExtrude","CAP_FACE",FACE,{"disambiguationData":[OSD([subQ0,sQuery(id+"F0.wireOp",EDGE,"E4.3.0"),sQuery(id+"F0.wireOp",EDGE,"E4.3.1")])],"isStart":true})]})]});}
            var Q10;
            {var subQ0=sQuery(id+"F0.wireOp",EDGE,"E1");var subQ1=makeQuery(id+"F2.opExtrude","CAP_FACE",FACE,{"disambiguationData":[OSD([subQ0,sQuery(id+"F0.wireOp",EDGE,"E4.3.0"),sQuery(id+"F0.wireOp",EDGE,"E4.3.1")])],"isStart":true});var subQ2=makeQuery(id+"F2.opExtrude","CAP_FACE",FACE,{"disambiguationData":[OSD([subQ0,sQuery(id+"F0.wireOp",EDGE,"E4.2.0"),sQuery(id+"F0.wireOp",EDGE,"E4.2.1")])],"isStart":true});var subQ3=makeQuery(id+"F2.opExtrude","CAP_FACE",FACE,{"disambiguationData":[OSD([subQ0,sQuery(id+"F0.wireOp",EDGE,"E4.1.0"),sQuery(id+"F0.wireOp",EDGE,"E4.1.1")])],"isStart":true});var subQ4=sQuery(id+"F0.wireOp",EDGE,"E2");var subQ5=makeQuery(id+"F2.opExtrude","CAP_FACE",FACE,{"disambiguationData":[OSD([subQ0,subQ4,sQuery(id+"F0.wireOp",EDGE,"E3")])],"isStart":true});var subQ6=sQuery(id+"F0.wireOp",EDGE,"E4.4.0");var subQ7=makeQuery(id+"F2.opExtrude","CAP_FACE",FACE,{"disambiguationData":[OSD([subQ0,subQ6,sQuery(id+"F0.wireOp",EDGE,"E4.4.1")])],"isStart":true});var subQ8=makeQuery(id+"F1.opExtrude","CAP_FACE",FACE,{"disambiguationData":[OSD([sQuery(id+"F0.wireOp",EDGE,"E0"),subQ0])],"isStart":true});Q10=makeQuery(id+"F5.opChamfer","BLEND_EDGE",EDGE,{"blendedFrom":[makeQuery(id+"F2.boolean.opBoolean","SPLIT",EDGE,{"disambiguationData":[TD([makeQuery(id+"F2.opExtrude","SWEPT_FACE",FACE,{"disambiguationData":[OSD([subQ4])]})])],"derivedFrom":makeQuery(id+"F1.opExtrude","CAP_EDGE",EDGE,{"disambiguationData":[OSD([subQ0])],"isStart":true})}),makeQuery(id+"F2.boolean.opBoolean","MERGE",FACE,{"derivedFrom":[subQ8,subQ7,subQ5,subQ3,subQ2,subQ1]})],"blendedInto":[makeQuery(id+"F2.boolean.opBoolean","MERGE",FACE,{"derivedFrom":[subQ8,subQ7,subQ5,subQ3,subQ2,subQ1]})]});}
            var Q11;
            {var subQ0=sQuery(id+"F0.wireOp",EDGE,"E1");var subQ1=makeQuery(id+"F2.opExtrude","CAP_FACE",FACE,{"disambiguationData":[OSD([subQ0,sQuery(id+"F0.wireOp",EDGE,"E4.3.0"),sQuery(id+"F0.wireOp",EDGE,"E4.3.1")])],"isStart":true});var subQ2=makeQuery(id+"F2.opExtrude","CAP_FACE",FACE,{"disambiguationData":[OSD([subQ0,sQuery(id+"F0.wireOp",EDGE,"E4.2.0"),sQuery(id+"F0.wireOp",EDGE,"E4.2.1")])],"isStart":true});var subQ3=sQuery(id+"F0.wireOp",EDGE,"E4.1.1");var subQ4=makeQuery(id+"F2.opExtrude","CAP_FACE",FACE,{"disambiguationData":[OSD([subQ0,sQuery(id+"F0.wireOp",EDGE,"E4.1.0"),subQ3])],"isStart":true});var subQ5=sQuery(id+"F0.wireOp",EDGE,"E3");var subQ6=makeQuery(id+"F2.opExtrude","CAP_FACE",FACE,{"disambiguationData":[OSD([subQ0,sQuery(id+"F0.wireOp",EDGE,"E2"),subQ5])],"isStart":true});var subQ7=makeQuery(id+"F2.opExtrude","CAP_FACE",FACE,{"disambiguationData":[OSD([subQ0,sQuery(id+"F0.wireOp",EDGE,"E4.4.0"),sQuery(id+"F0.wireOp",EDGE,"E4.4.1")])],"isStart":true});var subQ8=makeQuery(id+"F1.opExtrude","CAP_FACE",FACE,{"disambiguationData":[OSD([sQuery(id+"F0.wireOp",EDGE,"E0"),subQ0])],"isStart":true});Q11=makeQuery(id+"F5.opChamfer","BLEND_EDGE",EDGE,{"blendedFrom":[makeQuery(id+"F2.boolean.opBoolean","SPLIT",EDGE,{"disambiguationData":[TD([makeQuery(id+"F2.opExtrude","SWEPT_FACE",FACE,{"disambiguationData":[OSD([subQ5])]})])],"derivedFrom":makeQuery(id+"F1.opExtrude","CAP_EDGE",EDGE,{"disambiguationData":[OSD([subQ0])],"isStart":true})}),makeQuery(id+"F2.boolean.opBoolean","MERGE",FACE,{"derivedFrom":[subQ8,subQ7,subQ6,subQ4,subQ2,subQ1]})],"blendedInto":[makeQuery(id+"F2.boolean.opBoolean","MERGE",FACE,{"derivedFrom":[subQ8,subQ7,subQ6,subQ4,subQ2,subQ1]})]});}
            var Q12;
            {var subQ0=sQuery(id+"F0.wireOp",EDGE,"E1");var subQ1=makeQuery(id+"F2.opExtrude","CAP_FACE",FACE,{"disambiguationData":[OSD([subQ0,sQuery(id+"F0.wireOp",EDGE,"E4.3.0"),sQuery(id+"F0.wireOp",EDGE,"E4.3.1")])],"isStart":true});var subQ2=sQuery(id+"F0.wireOp",EDGE,"E4.2.1");var subQ3=makeQuery(id+"F2.opExtrude","CAP_FACE",FACE,{"disambiguationData":[OSD([subQ0,sQuery(id+"F0.wireOp",EDGE,"E4.2.0"),subQ2])],"isStart":true});var subQ4=sQuery(id+"F0.wireOp",EDGE,"E4.1.0");var subQ5=makeQuery(id+"F2.opExtrude","CAP_FACE",FACE,{"disambiguationData":[OSD([subQ0,subQ4,sQuery(id+"F0.wireOp",EDGE,"E4.1.1")])],"isStart":true});var subQ6=makeQuery(id+"F2.opExtrude","CAP_FACE",FACE,{"disambiguationData":[OSD([subQ0,sQuery(id+"F0.wireOp",EDGE,"E2"),sQuery(id+"F0.wireOp",EDGE,"E3")])],"isStart":true});var subQ7=makeQuery(id+"F2.opExtrude","CAP_FACE",FACE,{"disambiguationData":[OSD([subQ0,sQuery(id+"F0.wireOp",EDGE,"E4.4.0"),sQuery(id+"F0.wireOp",EDGE,"E4.4.1")])],"isStart":true});var subQ8=makeQuery(id+"F1.opExtrude","CAP_FACE",FACE,{"disambiguationData":[OSD([sQuery(id+"F0.wireOp",EDGE,"E0"),subQ0])],"isStart":true});Q12=makeQuery(id+"F5.opChamfer","BLEND_EDGE",EDGE,{"blendedFrom":[makeQuery(id+"F2.boolean.opBoolean","SPLIT",EDGE,{"disambiguationData":[TD([makeQuery(id+"F2.opExtrude","SWEPT_FACE",FACE,{"disambiguationData":[OSD([subQ4])]})])],"derivedFrom":makeQuery(id+"F1.opExtrude","CAP_EDGE",EDGE,{"disambiguationData":[OSD([subQ0])],"isStart":true})}),makeQuery(id+"F2.boolean.opBoolean","MERGE",FACE,{"derivedFrom":[subQ8,subQ7,subQ6,subQ5,subQ3,subQ1]})],"blendedInto":[makeQuery(id+"F2.boolean.opBoolean","MERGE",FACE,{"derivedFrom":[subQ8,subQ7,subQ6,subQ5,subQ3,subQ1]})]});}
            var Q13;
            {var subQ0=sQuery(id+"F0.wireOp",EDGE,"E4.3.1");var subQ1=sQuery(id+"F0.wireOp",EDGE,"E1");var subQ2=makeQuery(id+"F2.opExtrude","CAP_FACE",FACE,{"disambiguationData":[OSD([subQ1,sQuery(id+"F0.wireOp",EDGE,"E4.3.0"),subQ0])],"isStart":true});var subQ3=sQuery(id+"F0.wireOp",EDGE,"E4.2.0");var subQ4=makeQuery(id+"F2.opExtrude","CAP_FACE",FACE,{"disambiguationData":[OSD([subQ1,subQ3,sQuery(id+"F0.wireOp",EDGE,"E4.2.1")])],"isStart":true});var subQ5=makeQuery(id+"F2.opExtrude","CAP_FACE",FACE,{"disambiguationData":[OSD([subQ1,sQuery(id+"F0.wireOp",EDGE,"E4.1.0"),sQuery(id+"F0.wireOp",EDGE,"E4.1.1")])],"isStart":true});var subQ6=makeQuery(id+"F2.opExtrude","CAP_FACE",FACE,{"disambiguationData":[OSD([subQ1,sQuery(id+"F0.wireOp",EDGE,"E2"),sQuery(id+"F0.wireOp",EDGE,"E3")])],"isStart":true});var subQ7=makeQuery(id+"F2.opExtrude","CAP_FACE",FACE,{"disambiguationData":[OSD([subQ1,sQuery(id+"F0.wireOp",EDGE,"E4.4.0"),sQuery(id+"F0.wireOp",EDGE,"E4.4.1")])],"isStart":true});var subQ8=makeQuery(id+"F1.opExtrude","CAP_FACE",FACE,{"disambiguationData":[OSD([sQuery(id+"F0.wireOp",EDGE,"E0"),subQ1])],"isStart":true});Q13=makeQuery(id+"F5.opChamfer","BLEND_EDGE",EDGE,{"blendedFrom":[makeQuery(id+"F2.boolean.opBoolean","SPLIT",EDGE,{"disambiguationData":[TD([makeQuery(id+"F2.opExtrude","SWEPT_FACE",FACE,{"disambiguationData":[OSD([subQ3])]})])],"derivedFrom":makeQuery(id+"F1.opExtrude","CAP_EDGE",EDGE,{"disambiguationData":[OSD([subQ1])],"isStart":true})}),makeQuery(id+"F2.boolean.opBoolean","MERGE",FACE,{"derivedFrom":[subQ8,subQ7,subQ6,subQ5,subQ4,subQ2]})],"blendedInto":[makeQuery(id+"F2.boolean.opBoolean","MERGE",FACE,{"derivedFrom":[subQ8,subQ7,subQ6,subQ5,subQ4,subQ2]})]});}
            var Q14;
            {var subQ0=sQuery(id+"F0.wireOp",EDGE,"E4.3.0");var subQ1=sQuery(id+"F0.wireOp",EDGE,"E1");var subQ2=makeQuery(id+"F2.opExtrude","CAP_FACE",FACE,{"disambiguationData":[OSD([subQ1,subQ0,sQuery(id+"F0.wireOp",EDGE,"E4.3.1")])],"isStart":true});var subQ3=makeQuery(id+"F2.opExtrude","CAP_FACE",FACE,{"disambiguationData":[OSD([subQ1,sQuery(id+"F0.wireOp",EDGE,"E4.2.0"),sQuery(id+"F0.wireOp",EDGE,"E4.2.1")])],"isStart":true});var subQ4=makeQuery(id+"F2.opExtrude","CAP_FACE",FACE,{"disambiguationData":[OSD([subQ1,sQuery(id+"F0.wireOp",EDGE,"E4.1.0"),sQuery(id+"F0.wireOp",EDGE,"E4.1.1")])],"isStart":true});var subQ5=makeQuery(id+"F2.opExtrude","CAP_FACE",FACE,{"disambiguationData":[OSD([subQ1,sQuery(id+"F0.wireOp",EDGE,"E2"),sQuery(id+"F0.wireOp",EDGE,"E3")])],"isStart":true});var subQ6=sQuery(id+"F0.wireOp",EDGE,"E4.4.1");var subQ7=makeQuery(id+"F2.opExtrude","CAP_FACE",FACE,{"disambiguationData":[OSD([subQ1,sQuery(id+"F0.wireOp",EDGE,"E4.4.0"),subQ6])],"isStart":true});var subQ8=makeQuery(id+"F1.opExtrude","CAP_FACE",FACE,{"disambiguationData":[OSD([sQuery(id+"F0.wireOp",EDGE,"E0"),subQ1])],"isStart":true});Q14=makeQuery(id+"F5.opChamfer","BLEND_EDGE",EDGE,{"blendedFrom":[makeQuery(id+"F2.boolean.opBoolean","SPLIT",EDGE,{"disambiguationData":[TD([makeQuery(id+"F2.opExtrude","SWEPT_FACE",FACE,{"disambiguationData":[OSD([subQ0])]})])],"derivedFrom":makeQuery(id+"F1.opExtrude","CAP_EDGE",EDGE,{"disambiguationData":[OSD([subQ1])],"isStart":true})}),makeQuery(id+"F2.boolean.opBoolean","MERGE",FACE,{"derivedFrom":[subQ8,subQ7,subQ5,subQ4,subQ3,subQ2]})],"blendedInto":[makeQuery(id+"F2.boolean.opBoolean","MERGE",FACE,{"derivedFrom":[subQ8,subQ7,subQ5,subQ4,subQ3,subQ2]})]});}
            chamfer(context, id + "F6", {"entities" : qUnion([Q0, Q1, Q2, Q3, Q4, Q5, Q6, Q7, Q8, Q9, Q10, Q11, Q12, Q13, Q14]), "width" : 5 * mm, "tangentPropagation" : true});
        }
        {
            var Q0;
            {var subQ0=sQuery(id+"F0.wireOp",EDGE,"E1");var subQ1=makeQuery(id+"F2.opExtrude","CAP_FACE",FACE,{"disambiguationData":[OSD([subQ0,sQuery(id+"F0.wireOp",EDGE,"E4.3.0"),sQuery(id+"F0.wireOp",EDGE,"E4.3.1")])],"isStart":true});var subQ2=makeQuery(id+"F2.opExtrude","CAP_FACE",FACE,{"disambiguationData":[OSD([subQ0,sQuery(id+"F0.wireOp",EDGE,"E4.2.0"),sQuery(id+"F0.wireOp",EDGE,"E4.2.1")])],"isStart":true});var subQ3=makeQuery(id+"F2.opExtrude","CAP_FACE",FACE,{"disambiguationData":[OSD([subQ0,sQuery(id+"F0.wireOp",EDGE,"E4.1.0"),sQuery(id+"F0.wireOp",EDGE,"E4.1.1")])],"isStart":true});var subQ4=sQuery(id+"F0.wireOp",EDGE,"E2");var subQ5=makeQuery(id+"F2.opExtrude","CAP_FACE",FACE,{"disambiguationData":[OSD([subQ0,subQ4,sQuery(id+"F0.wireOp",EDGE,"E3")])],"isStart":true});var subQ6=sQuery(id+"F0.wireOp",EDGE,"E4.4.0");var subQ7=makeQuery(id+"F2.opExtrude","CAP_FACE",FACE,{"disambiguationData":[OSD([subQ0,subQ6,sQuery(id+"F0.wireOp",EDGE,"E4.4.1")])],"isStart":true});var subQ8=makeQuery(id+"F1.opExtrude","CAP_FACE",FACE,{"disambiguationData":[OSD([sQuery(id+"F0.wireOp",EDGE,"E0"),subQ0])],"isStart":true});var subQ9=makeQuery(id+"F2.boolean.opBoolean","MERGE",FACE,{"derivedFrom":[subQ8,subQ7,subQ5,subQ3,subQ2,subQ1]});Q0=makeQuery(id+"F6.opChamfer","BLEND_EDGE",EDGE,{"blendedFrom":[makeQuery(id+"F5.opChamfer","BLEND_EDGE",EDGE,{"blendedFrom":[makeQuery(id+"F2.boolean.opBoolean","SPLIT",EDGE,{"disambiguationData":[TD([makeQuery(id+"F2.opExtrude","SWEPT_FACE",FACE,{"disambiguationData":[OSD([subQ4])]})])],"derivedFrom":makeQuery(id+"F1.opExtrude","CAP_EDGE",EDGE,{"disambiguationData":[OSD([subQ0])],"isStart":true})}),subQ9],"blendedInto":[subQ9]}),subQ9],"blendedInto":[subQ9]});}
            var Q1;
            {var subQ0=sQuery(id+"F0.wireOp",EDGE,"E1");var subQ1=sQuery(id+"F0.wireOp",EDGE,"E2");var subQ2=makeQuery(id+"F2.boolean.opBoolean","MERGE",FACE,{"derivedFrom":[makeQuery(id+"F1.opExtrude","CAP_FACE",FACE,{"disambiguationData":[OSD([sQuery(id+"F0.wireOp",EDGE,"E0"),subQ0])],"isStart":true}),makeQuery(id+"F2.opExtrude","CAP_FACE",FACE,{"disambiguationData":[OSD([subQ0,sQuery(id+"F0.wireOp",EDGE,"E4.4.0"),sQuery(id+"F0.wireOp",EDGE,"E4.4.1")])],"isStart":true}),makeQuery(id+"F2.opExtrude","CAP_FACE",FACE,{"disambiguationData":[OSD([subQ0,subQ1,sQuery(id+"F0.wireOp",EDGE,"E3")])],"isStart":true}),makeQuery(id+"F2.opExtrude","CAP_FACE",FACE,{"disambiguationData":[OSD([subQ0,sQuery(id+"F0.wireOp",EDGE,"E4.1.0"),sQuery(id+"F0.wireOp",EDGE,"E4.1.1")])],"isStart":true}),makeQuery(id+"F2.opExtrude","CAP_FACE",FACE,{"disambiguationData":[OSD([subQ0,sQuery(id+"F0.wireOp",EDGE,"E4.2.0"),sQuery(id+"F0.wireOp",EDGE,"E4.2.1")])],"isStart":true}),makeQuery(id+"F2.opExtrude","CAP_FACE",FACE,{"disambiguationData":[OSD([subQ0,sQuery(id+"F0.wireOp",EDGE,"E4.3.0"),sQuery(id+"F0.wireOp",EDGE,"E4.3.1")])],"isStart":true})]});Q1=makeQuery(id+"F6.opChamfer","BLEND_EDGE",EDGE,{"blendedFrom":[makeQuery(id+"F5.opChamfer","BLEND_EDGE",EDGE,{"blendedFrom":[makeQuery(id+"F2.opExtrude","CAP_EDGE",EDGE,{"disambiguationData":[OSD([subQ1])],"isStart":true}),subQ2],"blendedInto":[subQ2]}),subQ2],"blendedInto":[subQ2]});}
            var Q2;
            {var subQ0=sQuery(id+"F0.wireOp",EDGE,"E1");var subQ1=makeQuery(id+"F2.opExtrude","CAP_FACE",FACE,{"disambiguationData":[OSD([subQ0,sQuery(id+"F0.wireOp",EDGE,"E4.3.0"),sQuery(id+"F0.wireOp",EDGE,"E4.3.1")])],"isStart":true});var subQ2=makeQuery(id+"F2.opExtrude","CAP_FACE",FACE,{"disambiguationData":[OSD([subQ0,sQuery(id+"F0.wireOp",EDGE,"E4.2.0"),sQuery(id+"F0.wireOp",EDGE,"E4.2.1")])],"isStart":true});var subQ3=sQuery(id+"F0.wireOp",EDGE,"E4.1.1");var subQ4=makeQuery(id+"F2.opExtrude","CAP_FACE",FACE,{"disambiguationData":[OSD([subQ0,sQuery(id+"F0.wireOp",EDGE,"E4.1.0"),subQ3])],"isStart":true});var subQ5=sQuery(id+"F0.wireOp",EDGE,"E3");var subQ6=makeQuery(id+"F2.opExtrude","CAP_FACE",FACE,{"disambiguationData":[OSD([subQ0,sQuery(id+"F0.wireOp",EDGE,"E2"),subQ5])],"isStart":true});var subQ7=makeQuery(id+"F2.opExtrude","CAP_FACE",FACE,{"disambiguationData":[OSD([subQ0,sQuery(id+"F0.wireOp",EDGE,"E4.4.0"),sQuery(id+"F0.wireOp",EDGE,"E4.4.1")])],"isStart":true});var subQ8=makeQuery(id+"F1.opExtrude","CAP_FACE",FACE,{"disambiguationData":[OSD([sQuery(id+"F0.wireOp",EDGE,"E0"),subQ0])],"isStart":true});var subQ9=makeQuery(id+"F2.boolean.opBoolean","MERGE",FACE,{"derivedFrom":[subQ8,subQ7,subQ6,subQ4,subQ2,subQ1]});Q2=makeQuery(id+"F6.opChamfer","BLEND_EDGE",EDGE,{"blendedFrom":[makeQuery(id+"F5.opChamfer","BLEND_EDGE",EDGE,{"blendedFrom":[makeQuery(id+"F2.boolean.opBoolean","SPLIT",EDGE,{"disambiguationData":[TD([makeQuery(id+"F2.opExtrude","SWEPT_FACE",FACE,{"disambiguationData":[OSD([subQ5])]})])],"derivedFrom":makeQuery(id+"F1.opExtrude","CAP_EDGE",EDGE,{"disambiguationData":[OSD([subQ0])],"isStart":true})}),subQ9],"blendedInto":[subQ9]}),subQ9],"blendedInto":[subQ9]});}
            var Q3;
            {var subQ0=sQuery(id+"F0.wireOp",EDGE,"E1");var subQ1=sQuery(id+"F0.wireOp",EDGE,"E4.1.1");var subQ2=makeQuery(id+"F2.boolean.opBoolean","MERGE",FACE,{"derivedFrom":[makeQuery(id+"F1.opExtrude","CAP_FACE",FACE,{"disambiguationData":[OSD([sQuery(id+"F0.wireOp",EDGE,"E0"),subQ0])],"isStart":true}),makeQuery(id+"F2.opExtrude","CAP_FACE",FACE,{"disambiguationData":[OSD([subQ0,sQuery(id+"F0.wireOp",EDGE,"E4.4.0"),sQuery(id+"F0.wireOp",EDGE,"E4.4.1")])],"isStart":true}),makeQuery(id+"F2.opExtrude","CAP_FACE",FACE,{"disambiguationData":[OSD([subQ0,sQuery(id+"F0.wireOp",EDGE,"E2"),sQuery(id+"F0.wireOp",EDGE,"E3")])],"isStart":true}),makeQuery(id+"F2.opExtrude","CAP_FACE",FACE,{"disambiguationData":[OSD([subQ0,sQuery(id+"F0.wireOp",EDGE,"E4.1.0"),subQ1])],"isStart":true}),makeQuery(id+"F2.opExtrude","CAP_FACE",FACE,{"disambiguationData":[OSD([subQ0,sQuery(id+"F0.wireOp",EDGE,"E4.2.0"),sQuery(id+"F0.wireOp",EDGE,"E4.2.1")])],"isStart":true}),makeQuery(id+"F2.opExtrude","CAP_FACE",FACE,{"disambiguationData":[OSD([subQ0,sQuery(id+"F0.wireOp",EDGE,"E4.3.0"),sQuery(id+"F0.wireOp",EDGE,"E4.3.1")])],"isStart":true})]});Q3=makeQuery(id+"F6.opChamfer","BLEND_EDGE",EDGE,{"blendedFrom":[makeQuery(id+"F5.opChamfer","BLEND_EDGE",EDGE,{"blendedFrom":[makeQuery(id+"F2.opExtrude","CAP_EDGE",EDGE,{"disambiguationData":[OSD([subQ1])],"isStart":true}),subQ2],"blendedInto":[subQ2]}),subQ2],"blendedInto":[subQ2]});}
            var Q4;
            {var subQ0=sQuery(id+"F0.wireOp",EDGE,"E1");var subQ1=makeQuery(id+"F2.opExtrude","CAP_FACE",FACE,{"disambiguationData":[OSD([subQ0,sQuery(id+"F0.wireOp",EDGE,"E4.3.0"),sQuery(id+"F0.wireOp",EDGE,"E4.3.1")])],"isStart":true});var subQ2=sQuery(id+"F0.wireOp",EDGE,"E4.2.1");var subQ3=makeQuery(id+"F2.opExtrude","CAP_FACE",FACE,{"disambiguationData":[OSD([subQ0,sQuery(id+"F0.wireOp",EDGE,"E4.2.0"),subQ2])],"isStart":true});var subQ4=sQuery(id+"F0.wireOp",EDGE,"E4.1.0");var subQ5=makeQuery(id+"F2.opExtrude","CAP_FACE",FACE,{"disambiguationData":[OSD([subQ0,subQ4,sQuery(id+"F0.wireOp",EDGE,"E4.1.1")])],"isStart":true});var subQ6=makeQuery(id+"F2.opExtrude","CAP_FACE",FACE,{"disambiguationData":[OSD([subQ0,sQuery(id+"F0.wireOp",EDGE,"E2"),sQuery(id+"F0.wireOp",EDGE,"E3")])],"isStart":true});var subQ7=makeQuery(id+"F2.opExtrude","CAP_FACE",FACE,{"disambiguationData":[OSD([subQ0,sQuery(id+"F0.wireOp",EDGE,"E4.4.0"),sQuery(id+"F0.wireOp",EDGE,"E4.4.1")])],"isStart":true});var subQ8=makeQuery(id+"F1.opExtrude","CAP_FACE",FACE,{"disambiguationData":[OSD([sQuery(id+"F0.wireOp",EDGE,"E0"),subQ0])],"isStart":true});var subQ9=makeQuery(id+"F2.boolean.opBoolean","MERGE",FACE,{"derivedFrom":[subQ8,subQ7,subQ6,subQ5,subQ3,subQ1]});Q4=makeQuery(id+"F6.opChamfer","BLEND_EDGE",EDGE,{"blendedFrom":[makeQuery(id+"F5.opChamfer","BLEND_EDGE",EDGE,{"blendedFrom":[makeQuery(id+"F2.boolean.opBoolean","SPLIT",EDGE,{"disambiguationData":[TD([makeQuery(id+"F2.opExtrude","SWEPT_FACE",FACE,{"disambiguationData":[OSD([subQ4])]})])],"derivedFrom":makeQuery(id+"F1.opExtrude","CAP_EDGE",EDGE,{"disambiguationData":[OSD([subQ0])],"isStart":true})}),subQ9],"blendedInto":[subQ9]}),subQ9],"blendedInto":[subQ9]});}
            var Q5;
            {var subQ0=sQuery(id+"F0.wireOp",EDGE,"E1");var subQ1=sQuery(id+"F0.wireOp",EDGE,"E4.2.1");var subQ2=makeQuery(id+"F2.boolean.opBoolean","MERGE",FACE,{"derivedFrom":[makeQuery(id+"F1.opExtrude","CAP_FACE",FACE,{"disambiguationData":[OSD([sQuery(id+"F0.wireOp",EDGE,"E0"),subQ0])],"isStart":true}),makeQuery(id+"F2.opExtrude","CAP_FACE",FACE,{"disambiguationData":[OSD([subQ0,sQuery(id+"F0.wireOp",EDGE,"E4.4.0"),sQuery(id+"F0.wireOp",EDGE,"E4.4.1")])],"isStart":true}),makeQuery(id+"F2.opExtrude","CAP_FACE",FACE,{"disambiguationData":[OSD([subQ0,sQuery(id+"F0.wireOp",EDGE,"E2"),sQuery(id+"F0.wireOp",EDGE,"E3")])],"isStart":true}),makeQuery(id+"F2.opExtrude","CAP_FACE",FACE,{"disambiguationData":[OSD([subQ0,sQuery(id+"F0.wireOp",EDGE,"E4.1.0"),sQuery(id+"F0.wireOp",EDGE,"E4.1.1")])],"isStart":true}),makeQuery(id+"F2.opExtrude","CAP_FACE",FACE,{"disambiguationData":[OSD([subQ0,sQuery(id+"F0.wireOp",EDGE,"E4.2.0"),subQ1])],"isStart":true}),makeQuery(id+"F2.opExtrude","CAP_FACE",FACE,{"disambiguationData":[OSD([subQ0,sQuery(id+"F0.wireOp",EDGE,"E4.3.0"),sQuery(id+"F0.wireOp",EDGE,"E4.3.1")])],"isStart":true})]});Q5=makeQuery(id+"F6.opChamfer","BLEND_EDGE",EDGE,{"blendedFrom":[makeQuery(id+"F5.opChamfer","BLEND_EDGE",EDGE,{"blendedFrom":[makeQuery(id+"F2.opExtrude","CAP_EDGE",EDGE,{"disambiguationData":[OSD([subQ1])],"isStart":true}),subQ2],"blendedInto":[subQ2]}),subQ2],"blendedInto":[subQ2]});}
            var Q6;
            {var subQ0=sQuery(id+"F0.wireOp",EDGE,"E4.3.1");var subQ1=sQuery(id+"F0.wireOp",EDGE,"E1");var subQ2=makeQuery(id+"F2.opExtrude","CAP_FACE",FACE,{"disambiguationData":[OSD([subQ1,sQuery(id+"F0.wireOp",EDGE,"E4.3.0"),subQ0])],"isStart":true});var subQ3=sQuery(id+"F0.wireOp",EDGE,"E4.2.0");var subQ4=makeQuery(id+"F2.opExtrude","CAP_FACE",FACE,{"disambiguationData":[OSD([subQ1,subQ3,sQuery(id+"F0.wireOp",EDGE,"E4.2.1")])],"isStart":true});var subQ5=makeQuery(id+"F2.opExtrude","CAP_FACE",FACE,{"disambiguationData":[OSD([subQ1,sQuery(id+"F0.wireOp",EDGE,"E4.1.0"),sQuery(id+"F0.wireOp",EDGE,"E4.1.1")])],"isStart":true});var subQ6=makeQuery(id+"F2.opExtrude","CAP_FACE",FACE,{"disambiguationData":[OSD([subQ1,sQuery(id+"F0.wireOp",EDGE,"E2"),sQuery(id+"F0.wireOp",EDGE,"E3")])],"isStart":true});var subQ7=makeQuery(id+"F2.opExtrude","CAP_FACE",FACE,{"disambiguationData":[OSD([subQ1,sQuery(id+"F0.wireOp",EDGE,"E4.4.0"),sQuery(id+"F0.wireOp",EDGE,"E4.4.1")])],"isStart":true});var subQ8=makeQuery(id+"F1.opExtrude","CAP_FACE",FACE,{"disambiguationData":[OSD([sQuery(id+"F0.wireOp",EDGE,"E0"),subQ1])],"isStart":true});var subQ9=makeQuery(id+"F2.boolean.opBoolean","MERGE",FACE,{"derivedFrom":[subQ8,subQ7,subQ6,subQ5,subQ4,subQ2]});Q6=makeQuery(id+"F6.opChamfer","BLEND_EDGE",EDGE,{"blendedFrom":[makeQuery(id+"F5.opChamfer","BLEND_EDGE",EDGE,{"blendedFrom":[makeQuery(id+"F2.boolean.opBoolean","SPLIT",EDGE,{"disambiguationData":[TD([makeQuery(id+"F2.opExtrude","SWEPT_FACE",FACE,{"disambiguationData":[OSD([subQ3])]})])],"derivedFrom":makeQuery(id+"F1.opExtrude","CAP_EDGE",EDGE,{"disambiguationData":[OSD([subQ1])],"isStart":true})}),subQ9],"blendedInto":[subQ9]}),subQ9],"blendedInto":[subQ9]});}
            var Q7;
            {var subQ0=sQuery(id+"F0.wireOp",EDGE,"E4.3.1");var subQ1=sQuery(id+"F0.wireOp",EDGE,"E1");var subQ2=makeQuery(id+"F2.boolean.opBoolean","MERGE",FACE,{"derivedFrom":[makeQuery(id+"F1.opExtrude","CAP_FACE",FACE,{"disambiguationData":[OSD([sQuery(id+"F0.wireOp",EDGE,"E0"),subQ1])],"isStart":true}),makeQuery(id+"F2.opExtrude","CAP_FACE",FACE,{"disambiguationData":[OSD([subQ1,sQuery(id+"F0.wireOp",EDGE,"E4.4.0"),sQuery(id+"F0.wireOp",EDGE,"E4.4.1")])],"isStart":true}),makeQuery(id+"F2.opExtrude","CAP_FACE",FACE,{"disambiguationData":[OSD([subQ1,sQuery(id+"F0.wireOp",EDGE,"E2"),sQuery(id+"F0.wireOp",EDGE,"E3")])],"isStart":true}),makeQuery(id+"F2.opExtrude","CAP_FACE",FACE,{"disambiguationData":[OSD([subQ1,sQuery(id+"F0.wireOp",EDGE,"E4.1.0"),sQuery(id+"F0.wireOp",EDGE,"E4.1.1")])],"isStart":true}),makeQuery(id+"F2.opExtrude","CAP_FACE",FACE,{"disambiguationData":[OSD([subQ1,sQuery(id+"F0.wireOp",EDGE,"E4.2.0"),sQuery(id+"F0.wireOp",EDGE,"E4.2.1")])],"isStart":true}),makeQuery(id+"F2.opExtrude","CAP_FACE",FACE,{"disambiguationData":[OSD([subQ1,sQuery(id+"F0.wireOp",EDGE,"E4.3.0"),subQ0])],"isStart":true})]});Q7=makeQuery(id+"F6.opChamfer","BLEND_EDGE",EDGE,{"blendedFrom":[makeQuery(id+"F5.opChamfer","BLEND_EDGE",EDGE,{"blendedFrom":[makeQuery(id+"F2.opExtrude","CAP_EDGE",EDGE,{"disambiguationData":[OSD([subQ0])],"isStart":true}),subQ2],"blendedInto":[subQ2]}),subQ2],"blendedInto":[subQ2]});}
            var Q8;
            {var subQ0=sQuery(id+"F0.wireOp",EDGE,"E4.3.0");var subQ1=sQuery(id+"F0.wireOp",EDGE,"E1");var subQ2=makeQuery(id+"F2.opExtrude","CAP_FACE",FACE,{"disambiguationData":[OSD([subQ1,subQ0,sQuery(id+"F0.wireOp",EDGE,"E4.3.1")])],"isStart":true});var subQ3=makeQuery(id+"F2.opExtrude","CAP_FACE",FACE,{"disambiguationData":[OSD([subQ1,sQuery(id+"F0.wireOp",EDGE,"E4.2.0"),sQuery(id+"F0.wireOp",EDGE,"E4.2.1")])],"isStart":true});var subQ4=makeQuery(id+"F2.opExtrude","CAP_FACE",FACE,{"disambiguationData":[OSD([subQ1,sQuery(id+"F0.wireOp",EDGE,"E4.1.0"),sQuery(id+"F0.wireOp",EDGE,"E4.1.1")])],"isStart":true});var subQ5=makeQuery(id+"F2.opExtrude","CAP_FACE",FACE,{"disambiguationData":[OSD([subQ1,sQuery(id+"F0.wireOp",EDGE,"E2"),sQuery(id+"F0.wireOp",EDGE,"E3")])],"isStart":true});var subQ6=sQuery(id+"F0.wireOp",EDGE,"E4.4.1");var subQ7=makeQuery(id+"F2.opExtrude","CAP_FACE",FACE,{"disambiguationData":[OSD([subQ1,sQuery(id+"F0.wireOp",EDGE,"E4.4.0"),subQ6])],"isStart":true});var subQ8=makeQuery(id+"F1.opExtrude","CAP_FACE",FACE,{"disambiguationData":[OSD([sQuery(id+"F0.wireOp",EDGE,"E0"),subQ1])],"isStart":true});var subQ9=makeQuery(id+"F2.boolean.opBoolean","MERGE",FACE,{"derivedFrom":[subQ8,subQ7,subQ5,subQ4,subQ3,subQ2]});Q8=makeQuery(id+"F6.opChamfer","BLEND_EDGE",EDGE,{"blendedFrom":[makeQuery(id+"F5.opChamfer","BLEND_EDGE",EDGE,{"blendedFrom":[makeQuery(id+"F2.boolean.opBoolean","SPLIT",EDGE,{"disambiguationData":[TD([makeQuery(id+"F2.opExtrude","SWEPT_FACE",FACE,{"disambiguationData":[OSD([subQ0])]})])],"derivedFrom":makeQuery(id+"F1.opExtrude","CAP_EDGE",EDGE,{"disambiguationData":[OSD([subQ1])],"isStart":true})}),subQ9],"blendedInto":[subQ9]}),subQ9],"blendedInto":[subQ9]});}
            var Q9;
            {var subQ0=sQuery(id+"F0.wireOp",EDGE,"E1");var subQ1=sQuery(id+"F0.wireOp",EDGE,"E4.4.1");var subQ2=makeQuery(id+"F2.boolean.opBoolean","MERGE",FACE,{"derivedFrom":[makeQuery(id+"F1.opExtrude","CAP_FACE",FACE,{"disambiguationData":[OSD([sQuery(id+"F0.wireOp",EDGE,"E0"),subQ0])],"isStart":true}),makeQuery(id+"F2.opExtrude","CAP_FACE",FACE,{"disambiguationData":[OSD([subQ0,sQuery(id+"F0.wireOp",EDGE,"E4.4.0"),subQ1])],"isStart":true}),makeQuery(id+"F2.opExtrude","CAP_FACE",FACE,{"disambiguationData":[OSD([subQ0,sQuery(id+"F0.wireOp",EDGE,"E2"),sQuery(id+"F0.wireOp",EDGE,"E3")])],"isStart":true}),makeQuery(id+"F2.opExtrude","CAP_FACE",FACE,{"disambiguationData":[OSD([subQ0,sQuery(id+"F0.wireOp",EDGE,"E4.1.0"),sQuery(id+"F0.wireOp",EDGE,"E4.1.1")])],"isStart":true}),makeQuery(id+"F2.opExtrude","CAP_FACE",FACE,{"disambiguationData":[OSD([subQ0,sQuery(id+"F0.wireOp",EDGE,"E4.2.0"),sQuery(id+"F0.wireOp",EDGE,"E4.2.1")])],"isStart":true}),makeQuery(id+"F2.opExtrude","CAP_FACE",FACE,{"disambiguationData":[OSD([subQ0,sQuery(id+"F0.wireOp",EDGE,"E4.3.0"),sQuery(id+"F0.wireOp",EDGE,"E4.3.1")])],"isStart":true})]});Q9=makeQuery(id+"F6.opChamfer","BLEND_EDGE",EDGE,{"blendedFrom":[makeQuery(id+"F5.opChamfer","BLEND_EDGE",EDGE,{"blendedFrom":[makeQuery(id+"F2.opExtrude","CAP_EDGE",EDGE,{"disambiguationData":[OSD([subQ1])],"isStart":true}),subQ2],"blendedInto":[subQ2]}),subQ2],"blendedInto":[subQ2]});}
            chamfer(context, id + "F7", {"entities" : qUnion([Q0, Q1, Q2, Q3, Q4, Q5, Q6, Q7, Q8, Q9]), "width" : 5 * mm, "tangentPropagation" : true});
        }
        {
            var Q0;
            {var subQ0=sQuery(id+"F0.wireOp",EDGE,"E1");var subQ1=sQuery(id+"F0.wireOp",EDGE,"E4.1.1");Q0=makeQuery(id+"F3.opChamfer","BLEND_EDGE",EDGE,{"blendedFrom":[makeQuery(id+"F2.opExtrude","CAP_EDGE",EDGE,{"disambiguationData":[OSD([subQ1])],"isStart":false}),makeQuery(id+"F2.boolean.opBoolean","MERGE",FACE,{"derivedFrom":[makeQuery(id+"F1.opExtrude","CAP_FACE",FACE,{"disambiguationData":[OSD([sQuery(id+"F0.wireOp",EDGE,"E0"),subQ0])],"isStart":false}),makeQuery(id+"F2.opExtrude","CAP_FACE",FACE,{"disambiguationData":[OSD([subQ0,sQuery(id+"F0.wireOp",EDGE,"E4.4.0"),sQuery(id+"F0.wireOp",EDGE,"E4.4.1")])],"isStart":false}),makeQuery(id+"F2.opExtrude","CAP_FACE",FACE,{"disambiguationData":[OSD([subQ0,sQuery(id+"F0.wireOp",EDGE,"E2"),sQuery(id+"F0.wireOp",EDGE,"E3")])],"isStart":false}),makeQuery(id+"F2.opExtrude","CAP_FACE",FACE,{"disambiguationData":[OSD([subQ0,sQuery(id+"F0.wireOp",EDGE,"E4.1.0"),subQ1])],"isStart":false}),makeQuery(id+"F2.opExtrude","CAP_FACE",FACE,{"disambiguationData":[OSD([subQ0,sQuery(id+"F0.wireOp",EDGE,"E4.2.0"),sQuery(id+"F0.wireOp",EDGE,"E4.2.1")])],"isStart":false}),makeQuery(id+"F2.opExtrude","CAP_FACE",FACE,{"disambiguationData":[OSD([subQ0,sQuery(id+"F0.wireOp",EDGE,"E4.3.0"),sQuery(id+"F0.wireOp",EDGE,"E4.3.1")])],"isStart":false})]})],"blendedInto":[makeQuery(id+"F2.boolean.opBoolean","MERGE",FACE,{"derivedFrom":[makeQuery(id+"F1.opExtrude","CAP_FACE",FACE,{"disambiguationData":[OSD([sQuery(id+"F0.wireOp",EDGE,"E0"),subQ0])],"isStart":false}),makeQuery(id+"F2.opExtrude","CAP_FACE",FACE,{"disambiguationData":[OSD([subQ0,sQuery(id+"F0.wireOp",EDGE,"E4.4.0"),sQuery(id+"F0.wireOp",EDGE,"E4.4.1")])],"isStart":false}),makeQuery(id+"F2.opExtrude","CAP_FACE",FACE,{"disambiguationData":[OSD([subQ0,sQuery(id+"F0.wireOp",EDGE,"E2"),sQuery(id+"F0.wireOp",EDGE,"E3")])],"isStart":false}),makeQuery(id+"F2.opExtrude","CAP_FACE",FACE,{"disambiguationData":[OSD([subQ0,sQuery(id+"F0.wireOp",EDGE,"E4.1.0"),subQ1])],"isStart":false}),makeQuery(id+"F2.opExtrude","CAP_FACE",FACE,{"disambiguationData":[OSD([subQ0,sQuery(id+"F0.wireOp",EDGE,"E4.2.0"),sQuery(id+"F0.wireOp",EDGE,"E4.2.1")])],"isStart":false}),makeQuery(id+"F2.opExtrude","CAP_FACE",FACE,{"disambiguationData":[OSD([subQ0,sQuery(id+"F0.wireOp",EDGE,"E4.3.0"),sQuery(id+"F0.wireOp",EDGE,"E4.3.1")])],"isStart":false})]})]});}
            var Q1;
            {var subQ0=sQuery(id+"F0.wireOp",EDGE,"E1");var subQ1=sQuery(id+"F0.wireOp",EDGE,"E4.1.0");Q1=makeQuery(id+"F3.opChamfer","BLEND_EDGE",EDGE,{"blendedFrom":[makeQuery(id+"F2.opExtrude","CAP_EDGE",EDGE,{"disambiguationData":[OSD([subQ1])],"isStart":false}),makeQuery(id+"F2.boolean.opBoolean","MERGE",FACE,{"derivedFrom":[makeQuery(id+"F1.opExtrude","CAP_FACE",FACE,{"disambiguationData":[OSD([sQuery(id+"F0.wireOp",EDGE,"E0"),subQ0])],"isStart":false}),makeQuery(id+"F2.opExtrude","CAP_FACE",FACE,{"disambiguationData":[OSD([subQ0,sQuery(id+"F0.wireOp",EDGE,"E4.4.0"),sQuery(id+"F0.wireOp",EDGE,"E4.4.1")])],"isStart":false}),makeQuery(id+"F2.opExtrude","CAP_FACE",FACE,{"disambiguationData":[OSD([subQ0,sQuery(id+"F0.wireOp",EDGE,"E2"),sQuery(id+"F0.wireOp",EDGE,"E3")])],"isStart":false}),makeQuery(id+"F2.opExtrude","CAP_FACE",FACE,{"disambiguationData":[OSD([subQ0,subQ1,sQuery(id+"F0.wireOp",EDGE,"E4.1.1")])],"isStart":false}),makeQuery(id+"F2.opExtrude","CAP_FACE",FACE,{"disambiguationData":[OSD([subQ0,sQuery(id+"F0.wireOp",EDGE,"E4.2.0"),sQuery(id+"F0.wireOp",EDGE,"E4.2.1")])],"isStart":false}),makeQuery(id+"F2.opExtrude","CAP_FACE",FACE,{"disambiguationData":[OSD([subQ0,sQuery(id+"F0.wireOp",EDGE,"E4.3.0"),sQuery(id+"F0.wireOp",EDGE,"E4.3.1")])],"isStart":false})]})],"blendedInto":[makeQuery(id+"F2.boolean.opBoolean","MERGE",FACE,{"derivedFrom":[makeQuery(id+"F1.opExtrude","CAP_FACE",FACE,{"disambiguationData":[OSD([sQuery(id+"F0.wireOp",EDGE,"E0"),subQ0])],"isStart":false}),makeQuery(id+"F2.opExtrude","CAP_FACE",FACE,{"disambiguationData":[OSD([subQ0,sQuery(id+"F0.wireOp",EDGE,"E4.4.0"),sQuery(id+"F0.wireOp",EDGE,"E4.4.1")])],"isStart":false}),makeQuery(id+"F2.opExtrude","CAP_FACE",FACE,{"disambiguationData":[OSD([subQ0,sQuery(id+"F0.wireOp",EDGE,"E2"),sQuery(id+"F0.wireOp",EDGE,"E3")])],"isStart":false}),makeQuery(id+"F2.opExtrude","CAP_FACE",FACE,{"disambiguationData":[OSD([subQ0,subQ1,sQuery(id+"F0.wireOp",EDGE,"E4.1.1")])],"isStart":false}),makeQuery(id+"F2.opExtrude","CAP_FACE",FACE,{"disambiguationData":[OSD([subQ0,sQuery(id+"F0.wireOp",EDGE,"E4.2.0"),sQuery(id+"F0.wireOp",EDGE,"E4.2.1")])],"isStart":false}),makeQuery(id+"F2.opExtrude","CAP_FACE",FACE,{"disambiguationData":[OSD([subQ0,sQuery(id+"F0.wireOp",EDGE,"E4.3.0"),sQuery(id+"F0.wireOp",EDGE,"E4.3.1")])],"isStart":false})]})]});}
            var Q2;
            {var subQ0=sQuery(id+"F0.wireOp",EDGE,"E1");var subQ1=sQuery(id+"F0.wireOp",EDGE,"E4.2.1");Q2=makeQuery(id+"F3.opChamfer","BLEND_EDGE",EDGE,{"blendedFrom":[makeQuery(id+"F2.opExtrude","CAP_EDGE",EDGE,{"disambiguationData":[OSD([subQ1])],"isStart":false}),makeQuery(id+"F2.boolean.opBoolean","MERGE",FACE,{"derivedFrom":[makeQuery(id+"F1.opExtrude","CAP_FACE",FACE,{"disambiguationData":[OSD([sQuery(id+"F0.wireOp",EDGE,"E0"),subQ0])],"isStart":false}),makeQuery(id+"F2.opExtrude","CAP_FACE",FACE,{"disambiguationData":[OSD([subQ0,sQuery(id+"F0.wireOp",EDGE,"E4.4.0"),sQuery(id+"F0.wireOp",EDGE,"E4.4.1")])],"isStart":false}),makeQuery(id+"F2.opExtrude","CAP_FACE",FACE,{"disambiguationData":[OSD([subQ0,sQuery(id+"F0.wireOp",EDGE,"E2"),sQuery(id+"F0.wireOp",EDGE,"E3")])],"isStart":false}),makeQuery(id+"F2.opExtrude","CAP_FACE",FACE,{"disambiguationData":[OSD([subQ0,sQuery(id+"F0.wireOp",EDGE,"E4.1.0"),sQuery(id+"F0.wireOp",EDGE,"E4.1.1")])],"isStart":false}),makeQuery(id+"F2.opExtrude","CAP_FACE",FACE,{"disambiguationData":[OSD([subQ0,sQuery(id+"F0.wireOp",EDGE,"E4.2.0"),subQ1])],"isStart":false}),makeQuery(id+"F2.opExtrude","CAP_FACE",FACE,{"disambiguationData":[OSD([subQ0,sQuery(id+"F0.wireOp",EDGE,"E4.3.0"),sQuery(id+"F0.wireOp",EDGE,"E4.3.1")])],"isStart":false})]})],"blendedInto":[makeQuery(id+"F2.boolean.opBoolean","MERGE",FACE,{"derivedFrom":[makeQuery(id+"F1.opExtrude","CAP_FACE",FACE,{"disambiguationData":[OSD([sQuery(id+"F0.wireOp",EDGE,"E0"),subQ0])],"isStart":false}),makeQuery(id+"F2.opExtrude","CAP_FACE",FACE,{"disambiguationData":[OSD([subQ0,sQuery(id+"F0.wireOp",EDGE,"E4.4.0"),sQuery(id+"F0.wireOp",EDGE,"E4.4.1")])],"isStart":false}),makeQuery(id+"F2.opExtrude","CAP_FACE",FACE,{"disambiguationData":[OSD([subQ0,sQuery(id+"F0.wireOp",EDGE,"E2"),sQuery(id+"F0.wireOp",EDGE,"E3")])],"isStart":false}),makeQuery(id+"F2.opExtrude","CAP_FACE",FACE,{"disambiguationData":[OSD([subQ0,sQuery(id+"F0.wireOp",EDGE,"E4.1.0"),sQuery(id+"F0.wireOp",EDGE,"E4.1.1")])],"isStart":false}),makeQuery(id+"F2.opExtrude","CAP_FACE",FACE,{"disambiguationData":[OSD([subQ0,sQuery(id+"F0.wireOp",EDGE,"E4.2.0"),subQ1])],"isStart":false}),makeQuery(id+"F2.opExtrude","CAP_FACE",FACE,{"disambiguationData":[OSD([subQ0,sQuery(id+"F0.wireOp",EDGE,"E4.3.0"),sQuery(id+"F0.wireOp",EDGE,"E4.3.1")])],"isStart":false})]})]});}
            var Q3;
            {var subQ0=sQuery(id+"F0.wireOp",EDGE,"E1");var subQ1=sQuery(id+"F0.wireOp",EDGE,"E4.2.0");Q3=makeQuery(id+"F3.opChamfer","BLEND_EDGE",EDGE,{"blendedFrom":[makeQuery(id+"F2.opExtrude","CAP_EDGE",EDGE,{"disambiguationData":[OSD([subQ1])],"isStart":false}),makeQuery(id+"F2.boolean.opBoolean","MERGE",FACE,{"derivedFrom":[makeQuery(id+"F1.opExtrude","CAP_FACE",FACE,{"disambiguationData":[OSD([sQuery(id+"F0.wireOp",EDGE,"E0"),subQ0])],"isStart":false}),makeQuery(id+"F2.opExtrude","CAP_FACE",FACE,{"disambiguationData":[OSD([subQ0,sQuery(id+"F0.wireOp",EDGE,"E4.4.0"),sQuery(id+"F0.wireOp",EDGE,"E4.4.1")])],"isStart":false}),makeQuery(id+"F2.opExtrude","CAP_FACE",FACE,{"disambiguationData":[OSD([subQ0,sQuery(id+"F0.wireOp",EDGE,"E2"),sQuery(id+"F0.wireOp",EDGE,"E3")])],"isStart":false}),makeQuery(id+"F2.opExtrude","CAP_FACE",FACE,{"disambiguationData":[OSD([subQ0,sQuery(id+"F0.wireOp",EDGE,"E4.1.0"),sQuery(id+"F0.wireOp",EDGE,"E4.1.1")])],"isStart":false}),makeQuery(id+"F2.opExtrude","CAP_FACE",FACE,{"disambiguationData":[OSD([subQ0,subQ1,sQuery(id+"F0.wireOp",EDGE,"E4.2.1")])],"isStart":false}),makeQuery(id+"F2.opExtrude","CAP_FACE",FACE,{"disambiguationData":[OSD([subQ0,sQuery(id+"F0.wireOp",EDGE,"E4.3.0"),sQuery(id+"F0.wireOp",EDGE,"E4.3.1")])],"isStart":false})]})],"blendedInto":[makeQuery(id+"F2.boolean.opBoolean","MERGE",FACE,{"derivedFrom":[makeQuery(id+"F1.opExtrude","CAP_FACE",FACE,{"disambiguationData":[OSD([sQuery(id+"F0.wireOp",EDGE,"E0"),subQ0])],"isStart":false}),makeQuery(id+"F2.opExtrude","CAP_FACE",FACE,{"disambiguationData":[OSD([subQ0,sQuery(id+"F0.wireOp",EDGE,"E4.4.0"),sQuery(id+"F0.wireOp",EDGE,"E4.4.1")])],"isStart":false}),makeQuery(id+"F2.opExtrude","CAP_FACE",FACE,{"disambiguationData":[OSD([subQ0,sQuery(id+"F0.wireOp",EDGE,"E2"),sQuery(id+"F0.wireOp",EDGE,"E3")])],"isStart":false}),makeQuery(id+"F2.opExtrude","CAP_FACE",FACE,{"disambiguationData":[OSD([subQ0,sQuery(id+"F0.wireOp",EDGE,"E4.1.0"),sQuery(id+"F0.wireOp",EDGE,"E4.1.1")])],"isStart":false}),makeQuery(id+"F2.opExtrude","CAP_FACE",FACE,{"disambiguationData":[OSD([subQ0,subQ1,sQuery(id+"F0.wireOp",EDGE,"E4.2.1")])],"isStart":false}),makeQuery(id+"F2.opExtrude","CAP_FACE",FACE,{"disambiguationData":[OSD([subQ0,sQuery(id+"F0.wireOp",EDGE,"E4.3.0"),sQuery(id+"F0.wireOp",EDGE,"E4.3.1")])],"isStart":false})]})]});}
            var Q4;
            {var subQ0=sQuery(id+"F0.wireOp",EDGE,"E4.3.1");var subQ1=sQuery(id+"F0.wireOp",EDGE,"E1");Q4=makeQuery(id+"F3.opChamfer","BLEND_EDGE",EDGE,{"blendedFrom":[makeQuery(id+"F2.opExtrude","CAP_EDGE",EDGE,{"disambiguationData":[OSD([subQ0])],"isStart":false}),makeQuery(id+"F2.boolean.opBoolean","MERGE",FACE,{"derivedFrom":[makeQuery(id+"F1.opExtrude","CAP_FACE",FACE,{"disambiguationData":[OSD([sQuery(id+"F0.wireOp",EDGE,"E0"),subQ1])],"isStart":false}),makeQuery(id+"F2.opExtrude","CAP_FACE",FACE,{"disambiguationData":[OSD([subQ1,sQuery(id+"F0.wireOp",EDGE,"E4.4.0"),sQuery(id+"F0.wireOp",EDGE,"E4.4.1")])],"isStart":false}),makeQuery(id+"F2.opExtrude","CAP_FACE",FACE,{"disambiguationData":[OSD([subQ1,sQuery(id+"F0.wireOp",EDGE,"E2"),sQuery(id+"F0.wireOp",EDGE,"E3")])],"isStart":false}),makeQuery(id+"F2.opExtrude","CAP_FACE",FACE,{"disambiguationData":[OSD([subQ1,sQuery(id+"F0.wireOp",EDGE,"E4.1.0"),sQuery(id+"F0.wireOp",EDGE,"E4.1.1")])],"isStart":false}),makeQuery(id+"F2.opExtrude","CAP_FACE",FACE,{"disambiguationData":[OSD([subQ1,sQuery(id+"F0.wireOp",EDGE,"E4.2.0"),sQuery(id+"F0.wireOp",EDGE,"E4.2.1")])],"isStart":false}),makeQuery(id+"F2.opExtrude","CAP_FACE",FACE,{"disambiguationData":[OSD([subQ1,sQuery(id+"F0.wireOp",EDGE,"E4.3.0"),subQ0])],"isStart":false})]})],"blendedInto":[makeQuery(id+"F2.boolean.opBoolean","MERGE",FACE,{"derivedFrom":[makeQuery(id+"F1.opExtrude","CAP_FACE",FACE,{"disambiguationData":[OSD([sQuery(id+"F0.wireOp",EDGE,"E0"),subQ1])],"isStart":false}),makeQuery(id+"F2.opExtrude","CAP_FACE",FACE,{"disambiguationData":[OSD([subQ1,sQuery(id+"F0.wireOp",EDGE,"E4.4.0"),sQuery(id+"F0.wireOp",EDGE,"E4.4.1")])],"isStart":false}),makeQuery(id+"F2.opExtrude","CAP_FACE",FACE,{"disambiguationData":[OSD([subQ1,sQuery(id+"F0.wireOp",EDGE,"E2"),sQuery(id+"F0.wireOp",EDGE,"E3")])],"isStart":false}),makeQuery(id+"F2.opExtrude","CAP_FACE",FACE,{"disambiguationData":[OSD([subQ1,sQuery(id+"F0.wireOp",EDGE,"E4.1.0"),sQuery(id+"F0.wireOp",EDGE,"E4.1.1")])],"isStart":false}),makeQuery(id+"F2.opExtrude","CAP_FACE",FACE,{"disambiguationData":[OSD([subQ1,sQuery(id+"F0.wireOp",EDGE,"E4.2.0"),sQuery(id+"F0.wireOp",EDGE,"E4.2.1")])],"isStart":false}),makeQuery(id+"F2.opExtrude","CAP_FACE",FACE,{"disambiguationData":[OSD([subQ1,sQuery(id+"F0.wireOp",EDGE,"E4.3.0"),subQ0])],"isStart":false})]})]});}
            var Q5;
            {var subQ0=sQuery(id+"F0.wireOp",EDGE,"E4.3.1");var subQ1=sQuery(id+"F0.wireOp",EDGE,"E1");var subQ2=makeQuery(id+"F2.opExtrude","CAP_FACE",FACE,{"disambiguationData":[OSD([subQ1,sQuery(id+"F0.wireOp",EDGE,"E4.3.0"),subQ0])],"isStart":false});var subQ3=sQuery(id+"F0.wireOp",EDGE,"E4.2.0");var subQ4=makeQuery(id+"F2.opExtrude","CAP_FACE",FACE,{"disambiguationData":[OSD([subQ1,subQ3,sQuery(id+"F0.wireOp",EDGE,"E4.2.1")])],"isStart":false});var subQ5=makeQuery(id+"F2.opExtrude","CAP_FACE",FACE,{"disambiguationData":[OSD([subQ1,sQuery(id+"F0.wireOp",EDGE,"E4.1.0"),sQuery(id+"F0.wireOp",EDGE,"E4.1.1")])],"isStart":false});var subQ6=makeQuery(id+"F2.opExtrude","CAP_FACE",FACE,{"disambiguationData":[OSD([subQ1,sQuery(id+"F0.wireOp",EDGE,"E2"),sQuery(id+"F0.wireOp",EDGE,"E3")])],"isStart":false});var subQ7=makeQuery(id+"F2.opExtrude","CAP_FACE",FACE,{"disambiguationData":[OSD([subQ1,sQuery(id+"F0.wireOp",EDGE,"E4.4.0"),sQuery(id+"F0.wireOp",EDGE,"E4.4.1")])],"isStart":false});var subQ8=makeQuery(id+"F1.opExtrude","CAP_FACE",FACE,{"disambiguationData":[OSD([sQuery(id+"F0.wireOp",EDGE,"E0"),subQ1])],"isStart":false});Q5=makeQuery(id+"F4.opChamfer","BLEND_EDGE",EDGE,{"blendedFrom":[makeQuery(id+"F2.boolean.opBoolean","SPLIT",EDGE,{"disambiguationData":[TD([makeQuery(id+"F2.opExtrude","SWEPT_FACE",FACE,{"disambiguationData":[OSD([subQ3])]})])],"derivedFrom":makeQuery(id+"F1.opExtrude","CAP_EDGE",EDGE,{"disambiguationData":[OSD([subQ1])],"isStart":false})}),makeQuery(id+"F2.boolean.opBoolean","MERGE",FACE,{"derivedFrom":[subQ8,subQ7,subQ6,subQ5,subQ4,subQ2]})],"blendedInto":[makeQuery(id+"F2.boolean.opBoolean","MERGE",FACE,{"derivedFrom":[subQ8,subQ7,subQ6,subQ5,subQ4,subQ2]})]});}
            var Q6;
            {var subQ0=sQuery(id+"F0.wireOp",EDGE,"E1");var subQ1=makeQuery(id+"F2.opExtrude","CAP_FACE",FACE,{"disambiguationData":[OSD([subQ0,sQuery(id+"F0.wireOp",EDGE,"E4.3.0"),sQuery(id+"F0.wireOp",EDGE,"E4.3.1")])],"isStart":false});var subQ2=sQuery(id+"F0.wireOp",EDGE,"E4.2.1");var subQ3=makeQuery(id+"F2.opExtrude","CAP_FACE",FACE,{"disambiguationData":[OSD([subQ0,sQuery(id+"F0.wireOp",EDGE,"E4.2.0"),subQ2])],"isStart":false});var subQ4=sQuery(id+"F0.wireOp",EDGE,"E4.1.0");var subQ5=makeQuery(id+"F2.opExtrude","CAP_FACE",FACE,{"disambiguationData":[OSD([subQ0,subQ4,sQuery(id+"F0.wireOp",EDGE,"E4.1.1")])],"isStart":false});var subQ6=makeQuery(id+"F2.opExtrude","CAP_FACE",FACE,{"disambiguationData":[OSD([subQ0,sQuery(id+"F0.wireOp",EDGE,"E2"),sQuery(id+"F0.wireOp",EDGE,"E3")])],"isStart":false});var subQ7=makeQuery(id+"F2.opExtrude","CAP_FACE",FACE,{"disambiguationData":[OSD([subQ0,sQuery(id+"F0.wireOp",EDGE,"E4.4.0"),sQuery(id+"F0.wireOp",EDGE,"E4.4.1")])],"isStart":false});var subQ8=makeQuery(id+"F1.opExtrude","CAP_FACE",FACE,{"disambiguationData":[OSD([sQuery(id+"F0.wireOp",EDGE,"E0"),subQ0])],"isStart":false});Q6=makeQuery(id+"F4.opChamfer","BLEND_EDGE",EDGE,{"blendedFrom":[makeQuery(id+"F2.boolean.opBoolean","SPLIT",EDGE,{"disambiguationData":[TD([makeQuery(id+"F2.opExtrude","SWEPT_FACE",FACE,{"disambiguationData":[OSD([subQ4])]})])],"derivedFrom":makeQuery(id+"F1.opExtrude","CAP_EDGE",EDGE,{"disambiguationData":[OSD([subQ0])],"isStart":false})}),makeQuery(id+"F2.boolean.opBoolean","MERGE",FACE,{"derivedFrom":[subQ8,subQ7,subQ6,subQ5,subQ3,subQ1]})],"blendedInto":[makeQuery(id+"F2.boolean.opBoolean","MERGE",FACE,{"derivedFrom":[subQ8,subQ7,subQ6,subQ5,subQ3,subQ1]})]});}
            var Q7;
            {var subQ0=sQuery(id+"F0.wireOp",EDGE,"E1");var subQ1=makeQuery(id+"F2.opExtrude","CAP_FACE",FACE,{"disambiguationData":[OSD([subQ0,sQuery(id+"F0.wireOp",EDGE,"E4.3.0"),sQuery(id+"F0.wireOp",EDGE,"E4.3.1")])],"isStart":false});var subQ2=makeQuery(id+"F2.opExtrude","CAP_FACE",FACE,{"disambiguationData":[OSD([subQ0,sQuery(id+"F0.wireOp",EDGE,"E4.2.0"),sQuery(id+"F0.wireOp",EDGE,"E4.2.1")])],"isStart":false});var subQ3=sQuery(id+"F0.wireOp",EDGE,"E4.1.1");var subQ4=makeQuery(id+"F2.opExtrude","CAP_FACE",FACE,{"disambiguationData":[OSD([subQ0,sQuery(id+"F0.wireOp",EDGE,"E4.1.0"),subQ3])],"isStart":false});var subQ5=sQuery(id+"F0.wireOp",EDGE,"E3");var subQ6=makeQuery(id+"F2.opExtrude","CAP_FACE",FACE,{"disambiguationData":[OSD([subQ0,sQuery(id+"F0.wireOp",EDGE,"E2"),subQ5])],"isStart":false});var subQ7=makeQuery(id+"F2.opExtrude","CAP_FACE",FACE,{"disambiguationData":[OSD([subQ0,sQuery(id+"F0.wireOp",EDGE,"E4.4.0"),sQuery(id+"F0.wireOp",EDGE,"E4.4.1")])],"isStart":false});var subQ8=makeQuery(id+"F1.opExtrude","CAP_FACE",FACE,{"disambiguationData":[OSD([sQuery(id+"F0.wireOp",EDGE,"E0"),subQ0])],"isStart":false});Q7=makeQuery(id+"F4.opChamfer","BLEND_EDGE",EDGE,{"blendedFrom":[makeQuery(id+"F2.boolean.opBoolean","SPLIT",EDGE,{"disambiguationData":[TD([makeQuery(id+"F2.opExtrude","SWEPT_FACE",FACE,{"disambiguationData":[OSD([subQ5])]})])],"derivedFrom":makeQuery(id+"F1.opExtrude","CAP_EDGE",EDGE,{"disambiguationData":[OSD([subQ0])],"isStart":false})}),makeQuery(id+"F2.boolean.opBoolean","MERGE",FACE,{"derivedFrom":[subQ8,subQ7,subQ6,subQ4,subQ2,subQ1]})],"blendedInto":[makeQuery(id+"F2.boolean.opBoolean","MERGE",FACE,{"derivedFrom":[subQ8,subQ7,subQ6,subQ4,subQ2,subQ1]})]});}
            var Q8;
            {var subQ0=sQuery(id+"F0.wireOp",EDGE,"E1");var subQ1=sQuery(id+"F0.wireOp",EDGE,"E3");Q8=makeQuery(id+"F3.opChamfer","BLEND_EDGE",EDGE,{"blendedFrom":[makeQuery(id+"F2.opExtrude","CAP_EDGE",EDGE,{"disambiguationData":[OSD([subQ1])],"isStart":false}),makeQuery(id+"F2.boolean.opBoolean","MERGE",FACE,{"derivedFrom":[makeQuery(id+"F1.opExtrude","CAP_FACE",FACE,{"disambiguationData":[OSD([sQuery(id+"F0.wireOp",EDGE,"E0"),subQ0])],"isStart":false}),makeQuery(id+"F2.opExtrude","CAP_FACE",FACE,{"disambiguationData":[OSD([subQ0,sQuery(id+"F0.wireOp",EDGE,"E4.4.0"),sQuery(id+"F0.wireOp",EDGE,"E4.4.1")])],"isStart":false}),makeQuery(id+"F2.opExtrude","CAP_FACE",FACE,{"disambiguationData":[OSD([subQ0,sQuery(id+"F0.wireOp",EDGE,"E2"),subQ1])],"isStart":false}),makeQuery(id+"F2.opExtrude","CAP_FACE",FACE,{"disambiguationData":[OSD([subQ0,sQuery(id+"F0.wireOp",EDGE,"E4.1.0"),sQuery(id+"F0.wireOp",EDGE,"E4.1.1")])],"isStart":false}),makeQuery(id+"F2.opExtrude","CAP_FACE",FACE,{"disambiguationData":[OSD([subQ0,sQuery(id+"F0.wireOp",EDGE,"E4.2.0"),sQuery(id+"F0.wireOp",EDGE,"E4.2.1")])],"isStart":false}),makeQuery(id+"F2.opExtrude","CAP_FACE",FACE,{"disambiguationData":[OSD([subQ0,sQuery(id+"F0.wireOp",EDGE,"E4.3.0"),sQuery(id+"F0.wireOp",EDGE,"E4.3.1")])],"isStart":false})]})],"blendedInto":[makeQuery(id+"F2.boolean.opBoolean","MERGE",FACE,{"derivedFrom":[makeQuery(id+"F1.opExtrude","CAP_FACE",FACE,{"disambiguationData":[OSD([sQuery(id+"F0.wireOp",EDGE,"E0"),subQ0])],"isStart":false}),makeQuery(id+"F2.opExtrude","CAP_FACE",FACE,{"disambiguationData":[OSD([subQ0,sQuery(id+"F0.wireOp",EDGE,"E4.4.0"),sQuery(id+"F0.wireOp",EDGE,"E4.4.1")])],"isStart":false}),makeQuery(id+"F2.opExtrude","CAP_FACE",FACE,{"disambiguationData":[OSD([subQ0,sQuery(id+"F0.wireOp",EDGE,"E2"),subQ1])],"isStart":false}),makeQuery(id+"F2.opExtrude","CAP_FACE",FACE,{"disambiguationData":[OSD([subQ0,sQuery(id+"F0.wireOp",EDGE,"E4.1.0"),sQuery(id+"F0.wireOp",EDGE,"E4.1.1")])],"isStart":false}),makeQuery(id+"F2.opExtrude","CAP_FACE",FACE,{"disambiguationData":[OSD([subQ0,sQuery(id+"F0.wireOp",EDGE,"E4.2.0"),sQuery(id+"F0.wireOp",EDGE,"E4.2.1")])],"isStart":false}),makeQuery(id+"F2.opExtrude","CAP_FACE",FACE,{"disambiguationData":[OSD([subQ0,sQuery(id+"F0.wireOp",EDGE,"E4.3.0"),sQuery(id+"F0.wireOp",EDGE,"E4.3.1")])],"isStart":false})]})]});}
            var Q9;
            {var subQ0=sQuery(id+"F0.wireOp",EDGE,"E1");var subQ1=sQuery(id+"F0.wireOp",EDGE,"E2");Q9=makeQuery(id+"F3.opChamfer","BLEND_EDGE",EDGE,{"blendedFrom":[makeQuery(id+"F2.opExtrude","CAP_EDGE",EDGE,{"disambiguationData":[OSD([subQ1])],"isStart":false}),makeQuery(id+"F2.boolean.opBoolean","MERGE",FACE,{"derivedFrom":[makeQuery(id+"F1.opExtrude","CAP_FACE",FACE,{"disambiguationData":[OSD([sQuery(id+"F0.wireOp",EDGE,"E0"),subQ0])],"isStart":false}),makeQuery(id+"F2.opExtrude","CAP_FACE",FACE,{"disambiguationData":[OSD([subQ0,sQuery(id+"F0.wireOp",EDGE,"E4.4.0"),sQuery(id+"F0.wireOp",EDGE,"E4.4.1")])],"isStart":false}),makeQuery(id+"F2.opExtrude","CAP_FACE",FACE,{"disambiguationData":[OSD([subQ0,subQ1,sQuery(id+"F0.wireOp",EDGE,"E3")])],"isStart":false}),makeQuery(id+"F2.opExtrude","CAP_FACE",FACE,{"disambiguationData":[OSD([subQ0,sQuery(id+"F0.wireOp",EDGE,"E4.1.0"),sQuery(id+"F0.wireOp",EDGE,"E4.1.1")])],"isStart":false}),makeQuery(id+"F2.opExtrude","CAP_FACE",FACE,{"disambiguationData":[OSD([subQ0,sQuery(id+"F0.wireOp",EDGE,"E4.2.0"),sQuery(id+"F0.wireOp",EDGE,"E4.2.1")])],"isStart":false}),makeQuery(id+"F2.opExtrude","CAP_FACE",FACE,{"disambiguationData":[OSD([subQ0,sQuery(id+"F0.wireOp",EDGE,"E4.3.0"),sQuery(id+"F0.wireOp",EDGE,"E4.3.1")])],"isStart":false})]})],"blendedInto":[makeQuery(id+"F2.boolean.opBoolean","MERGE",FACE,{"derivedFrom":[makeQuery(id+"F1.opExtrude","CAP_FACE",FACE,{"disambiguationData":[OSD([sQuery(id+"F0.wireOp",EDGE,"E0"),subQ0])],"isStart":false}),makeQuery(id+"F2.opExtrude","CAP_FACE",FACE,{"disambiguationData":[OSD([subQ0,sQuery(id+"F0.wireOp",EDGE,"E4.4.0"),sQuery(id+"F0.wireOp",EDGE,"E4.4.1")])],"isStart":false}),makeQuery(id+"F2.opExtrude","CAP_FACE",FACE,{"disambiguationData":[OSD([subQ0,subQ1,sQuery(id+"F0.wireOp",EDGE,"E3")])],"isStart":false}),makeQuery(id+"F2.opExtrude","CAP_FACE",FACE,{"disambiguationData":[OSD([subQ0,sQuery(id+"F0.wireOp",EDGE,"E4.1.0"),sQuery(id+"F0.wireOp",EDGE,"E4.1.1")])],"isStart":false}),makeQuery(id+"F2.opExtrude","CAP_FACE",FACE,{"disambiguationData":[OSD([subQ0,sQuery(id+"F0.wireOp",EDGE,"E4.2.0"),sQuery(id+"F0.wireOp",EDGE,"E4.2.1")])],"isStart":false}),makeQuery(id+"F2.opExtrude","CAP_FACE",FACE,{"disambiguationData":[OSD([subQ0,sQuery(id+"F0.wireOp",EDGE,"E4.3.0"),sQuery(id+"F0.wireOp",EDGE,"E4.3.1")])],"isStart":false})]})]});}
            var Q10;
            {var subQ0=sQuery(id+"F0.wireOp",EDGE,"E1");var subQ1=makeQuery(id+"F2.opExtrude","CAP_FACE",FACE,{"disambiguationData":[OSD([subQ0,sQuery(id+"F0.wireOp",EDGE,"E4.3.0"),sQuery(id+"F0.wireOp",EDGE,"E4.3.1")])],"isStart":false});var subQ2=makeQuery(id+"F2.opExtrude","CAP_FACE",FACE,{"disambiguationData":[OSD([subQ0,sQuery(id+"F0.wireOp",EDGE,"E4.2.0"),sQuery(id+"F0.wireOp",EDGE,"E4.2.1")])],"isStart":false});var subQ3=makeQuery(id+"F2.opExtrude","CAP_FACE",FACE,{"disambiguationData":[OSD([subQ0,sQuery(id+"F0.wireOp",EDGE,"E4.1.0"),sQuery(id+"F0.wireOp",EDGE,"E4.1.1")])],"isStart":false});var subQ4=sQuery(id+"F0.wireOp",EDGE,"E2");var subQ5=makeQuery(id+"F2.opExtrude","CAP_FACE",FACE,{"disambiguationData":[OSD([subQ0,subQ4,sQuery(id+"F0.wireOp",EDGE,"E3")])],"isStart":false});var subQ6=sQuery(id+"F0.wireOp",EDGE,"E4.4.0");var subQ7=makeQuery(id+"F2.opExtrude","CAP_FACE",FACE,{"disambiguationData":[OSD([subQ0,subQ6,sQuery(id+"F0.wireOp",EDGE,"E4.4.1")])],"isStart":false});var subQ8=makeQuery(id+"F1.opExtrude","CAP_FACE",FACE,{"disambiguationData":[OSD([sQuery(id+"F0.wireOp",EDGE,"E0"),subQ0])],"isStart":false});Q10=makeQuery(id+"F4.opChamfer","BLEND_EDGE",EDGE,{"blendedFrom":[makeQuery(id+"F2.boolean.opBoolean","SPLIT",EDGE,{"disambiguationData":[TD([makeQuery(id+"F2.opExtrude","SWEPT_FACE",FACE,{"disambiguationData":[OSD([subQ4])]})])],"derivedFrom":makeQuery(id+"F1.opExtrude","CAP_EDGE",EDGE,{"disambiguationData":[OSD([subQ0])],"isStart":false})}),makeQuery(id+"F2.boolean.opBoolean","MERGE",FACE,{"derivedFrom":[subQ8,subQ7,subQ5,subQ3,subQ2,subQ1]})],"blendedInto":[makeQuery(id+"F2.boolean.opBoolean","MERGE",FACE,{"derivedFrom":[subQ8,subQ7,subQ5,subQ3,subQ2,subQ1]})]});}
            var Q11;
            {var subQ0=sQuery(id+"F0.wireOp",EDGE,"E1");var subQ1=sQuery(id+"F0.wireOp",EDGE,"E4.4.0");Q11=makeQuery(id+"F3.opChamfer","BLEND_EDGE",EDGE,{"blendedFrom":[makeQuery(id+"F2.opExtrude","CAP_EDGE",EDGE,{"disambiguationData":[OSD([subQ1])],"isStart":false}),makeQuery(id+"F2.boolean.opBoolean","MERGE",FACE,{"derivedFrom":[makeQuery(id+"F1.opExtrude","CAP_FACE",FACE,{"disambiguationData":[OSD([sQuery(id+"F0.wireOp",EDGE,"E0"),subQ0])],"isStart":false}),makeQuery(id+"F2.opExtrude","CAP_FACE",FACE,{"disambiguationData":[OSD([subQ0,subQ1,sQuery(id+"F0.wireOp",EDGE,"E4.4.1")])],"isStart":false}),makeQuery(id+"F2.opExtrude","CAP_FACE",FACE,{"disambiguationData":[OSD([subQ0,sQuery(id+"F0.wireOp",EDGE,"E2"),sQuery(id+"F0.wireOp",EDGE,"E3")])],"isStart":false}),makeQuery(id+"F2.opExtrude","CAP_FACE",FACE,{"disambiguationData":[OSD([subQ0,sQuery(id+"F0.wireOp",EDGE,"E4.1.0"),sQuery(id+"F0.wireOp",EDGE,"E4.1.1")])],"isStart":false}),makeQuery(id+"F2.opExtrude","CAP_FACE",FACE,{"disambiguationData":[OSD([subQ0,sQuery(id+"F0.wireOp",EDGE,"E4.2.0"),sQuery(id+"F0.wireOp",EDGE,"E4.2.1")])],"isStart":false}),makeQuery(id+"F2.opExtrude","CAP_FACE",FACE,{"disambiguationData":[OSD([subQ0,sQuery(id+"F0.wireOp",EDGE,"E4.3.0"),sQuery(id+"F0.wireOp",EDGE,"E4.3.1")])],"isStart":false})]})],"blendedInto":[makeQuery(id+"F2.boolean.opBoolean","MERGE",FACE,{"derivedFrom":[makeQuery(id+"F1.opExtrude","CAP_FACE",FACE,{"disambiguationData":[OSD([sQuery(id+"F0.wireOp",EDGE,"E0"),subQ0])],"isStart":false}),makeQuery(id+"F2.opExtrude","CAP_FACE",FACE,{"disambiguationData":[OSD([subQ0,subQ1,sQuery(id+"F0.wireOp",EDGE,"E4.4.1")])],"isStart":false}),makeQuery(id+"F2.opExtrude","CAP_FACE",FACE,{"disambiguationData":[OSD([subQ0,sQuery(id+"F0.wireOp",EDGE,"E2"),sQuery(id+"F0.wireOp",EDGE,"E3")])],"isStart":false}),makeQuery(id+"F2.opExtrude","CAP_FACE",FACE,{"disambiguationData":[OSD([subQ0,sQuery(id+"F0.wireOp",EDGE,"E4.1.0"),sQuery(id+"F0.wireOp",EDGE,"E4.1.1")])],"isStart":false}),makeQuery(id+"F2.opExtrude","CAP_FACE",FACE,{"disambiguationData":[OSD([subQ0,sQuery(id+"F0.wireOp",EDGE,"E4.2.0"),sQuery(id+"F0.wireOp",EDGE,"E4.2.1")])],"isStart":false}),makeQuery(id+"F2.opExtrude","CAP_FACE",FACE,{"disambiguationData":[OSD([subQ0,sQuery(id+"F0.wireOp",EDGE,"E4.3.0"),sQuery(id+"F0.wireOp",EDGE,"E4.3.1")])],"isStart":false})]})]});}
            var Q12;
            {var subQ0=sQuery(id+"F0.wireOp",EDGE,"E1");var subQ1=sQuery(id+"F0.wireOp",EDGE,"E4.4.1");Q12=makeQuery(id+"F3.opChamfer","BLEND_EDGE",EDGE,{"blendedFrom":[makeQuery(id+"F2.opExtrude","CAP_EDGE",EDGE,{"disambiguationData":[OSD([subQ1])],"isStart":false}),makeQuery(id+"F2.boolean.opBoolean","MERGE",FACE,{"derivedFrom":[makeQuery(id+"F1.opExtrude","CAP_FACE",FACE,{"disambiguationData":[OSD([sQuery(id+"F0.wireOp",EDGE,"E0"),subQ0])],"isStart":false}),makeQuery(id+"F2.opExtrude","CAP_FACE",FACE,{"disambiguationData":[OSD([subQ0,sQuery(id+"F0.wireOp",EDGE,"E4.4.0"),subQ1])],"isStart":false}),makeQuery(id+"F2.opExtrude","CAP_FACE",FACE,{"disambiguationData":[OSD([subQ0,sQuery(id+"F0.wireOp",EDGE,"E2"),sQuery(id+"F0.wireOp",EDGE,"E3")])],"isStart":false}),makeQuery(id+"F2.opExtrude","CAP_FACE",FACE,{"disambiguationData":[OSD([subQ0,sQuery(id+"F0.wireOp",EDGE,"E4.1.0"),sQuery(id+"F0.wireOp",EDGE,"E4.1.1")])],"isStart":false}),makeQuery(id+"F2.opExtrude","CAP_FACE",FACE,{"disambiguationData":[OSD([subQ0,sQuery(id+"F0.wireOp",EDGE,"E4.2.0"),sQuery(id+"F0.wireOp",EDGE,"E4.2.1")])],"isStart":false}),makeQuery(id+"F2.opExtrude","CAP_FACE",FACE,{"disambiguationData":[OSD([subQ0,sQuery(id+"F0.wireOp",EDGE,"E4.3.0"),sQuery(id+"F0.wireOp",EDGE,"E4.3.1")])],"isStart":false})]})],"blendedInto":[makeQuery(id+"F2.boolean.opBoolean","MERGE",FACE,{"derivedFrom":[makeQuery(id+"F1.opExtrude","CAP_FACE",FACE,{"disambiguationData":[OSD([sQuery(id+"F0.wireOp",EDGE,"E0"),subQ0])],"isStart":false}),makeQuery(id+"F2.opExtrude","CAP_FACE",FACE,{"disambiguationData":[OSD([subQ0,sQuery(id+"F0.wireOp",EDGE,"E4.4.0"),subQ1])],"isStart":false}),makeQuery(id+"F2.opExtrude","CAP_FACE",FACE,{"disambiguationData":[OSD([subQ0,sQuery(id+"F0.wireOp",EDGE,"E2"),sQuery(id+"F0.wireOp",EDGE,"E3")])],"isStart":false}),makeQuery(id+"F2.opExtrude","CAP_FACE",FACE,{"disambiguationData":[OSD([subQ0,sQuery(id+"F0.wireOp",EDGE,"E4.1.0"),sQuery(id+"F0.wireOp",EDGE,"E4.1.1")])],"isStart":false}),makeQuery(id+"F2.opExtrude","CAP_FACE",FACE,{"disambiguationData":[OSD([subQ0,sQuery(id+"F0.wireOp",EDGE,"E4.2.0"),sQuery(id+"F0.wireOp",EDGE,"E4.2.1")])],"isStart":false}),makeQuery(id+"F2.opExtrude","CAP_FACE",FACE,{"disambiguationData":[OSD([subQ0,sQuery(id+"F0.wireOp",EDGE,"E4.3.0"),sQuery(id+"F0.wireOp",EDGE,"E4.3.1")])],"isStart":false})]})]});}
            var Q13;
            {var subQ0=sQuery(id+"F0.wireOp",EDGE,"E4.3.0");var subQ1=sQuery(id+"F0.wireOp",EDGE,"E1");var subQ2=makeQuery(id+"F2.opExtrude","CAP_FACE",FACE,{"disambiguationData":[OSD([subQ1,subQ0,sQuery(id+"F0.wireOp",EDGE,"E4.3.1")])],"isStart":false});var subQ3=makeQuery(id+"F2.opExtrude","CAP_FACE",FACE,{"disambiguationData":[OSD([subQ1,sQuery(id+"F0.wireOp",EDGE,"E4.2.0"),sQuery(id+"F0.wireOp",EDGE,"E4.2.1")])],"isStart":false});var subQ4=makeQuery(id+"F2.opExtrude","CAP_FACE",FACE,{"disambiguationData":[OSD([subQ1,sQuery(id+"F0.wireOp",EDGE,"E4.1.0"),sQuery(id+"F0.wireOp",EDGE,"E4.1.1")])],"isStart":false});var subQ5=makeQuery(id+"F2.opExtrude","CAP_FACE",FACE,{"disambiguationData":[OSD([subQ1,sQuery(id+"F0.wireOp",EDGE,"E2"),sQuery(id+"F0.wireOp",EDGE,"E3")])],"isStart":false});var subQ6=sQuery(id+"F0.wireOp",EDGE,"E4.4.1");var subQ7=makeQuery(id+"F2.opExtrude","CAP_FACE",FACE,{"disambiguationData":[OSD([subQ1,sQuery(id+"F0.wireOp",EDGE,"E4.4.0"),subQ6])],"isStart":false});var subQ8=makeQuery(id+"F1.opExtrude","CAP_FACE",FACE,{"disambiguationData":[OSD([sQuery(id+"F0.wireOp",EDGE,"E0"),subQ1])],"isStart":false});Q13=makeQuery(id+"F4.opChamfer","BLEND_EDGE",EDGE,{"blendedFrom":[makeQuery(id+"F2.boolean.opBoolean","SPLIT",EDGE,{"disambiguationData":[TD([makeQuery(id+"F2.opExtrude","SWEPT_FACE",FACE,{"disambiguationData":[OSD([subQ0])]})])],"derivedFrom":makeQuery(id+"F1.opExtrude","CAP_EDGE",EDGE,{"disambiguationData":[OSD([subQ1])],"isStart":false})}),makeQuery(id+"F2.boolean.opBoolean","MERGE",FACE,{"derivedFrom":[subQ8,subQ7,subQ5,subQ4,subQ3,subQ2]})],"blendedInto":[makeQuery(id+"F2.boolean.opBoolean","MERGE",FACE,{"derivedFrom":[subQ8,subQ7,subQ5,subQ4,subQ3,subQ2]})]});}
            var Q14;
            {var subQ0=sQuery(id+"F0.wireOp",EDGE,"E4.3.0");var subQ1=sQuery(id+"F0.wireOp",EDGE,"E1");Q14=makeQuery(id+"F3.opChamfer","BLEND_EDGE",EDGE,{"blendedFrom":[makeQuery(id+"F2.opExtrude","CAP_EDGE",EDGE,{"disambiguationData":[OSD([subQ0])],"isStart":false}),makeQuery(id+"F2.boolean.opBoolean","MERGE",FACE,{"derivedFrom":[makeQuery(id+"F1.opExtrude","CAP_FACE",FACE,{"disambiguationData":[OSD([sQuery(id+"F0.wireOp",EDGE,"E0"),subQ1])],"isStart":false}),makeQuery(id+"F2.opExtrude","CAP_FACE",FACE,{"disambiguationData":[OSD([subQ1,sQuery(id+"F0.wireOp",EDGE,"E4.4.0"),sQuery(id+"F0.wireOp",EDGE,"E4.4.1")])],"isStart":false}),makeQuery(id+"F2.opExtrude","CAP_FACE",FACE,{"disambiguationData":[OSD([subQ1,sQuery(id+"F0.wireOp",EDGE,"E2"),sQuery(id+"F0.wireOp",EDGE,"E3")])],"isStart":false}),makeQuery(id+"F2.opExtrude","CAP_FACE",FACE,{"disambiguationData":[OSD([subQ1,sQuery(id+"F0.wireOp",EDGE,"E4.1.0"),sQuery(id+"F0.wireOp",EDGE,"E4.1.1")])],"isStart":false}),makeQuery(id+"F2.opExtrude","CAP_FACE",FACE,{"disambiguationData":[OSD([subQ1,sQuery(id+"F0.wireOp",EDGE,"E4.2.0"),sQuery(id+"F0.wireOp",EDGE,"E4.2.1")])],"isStart":false}),makeQuery(id+"F2.opExtrude","CAP_FACE",FACE,{"disambiguationData":[OSD([subQ1,subQ0,sQuery(id+"F0.wireOp",EDGE,"E4.3.1")])],"isStart":false})]})],"blendedInto":[makeQuery(id+"F2.boolean.opBoolean","MERGE",FACE,{"derivedFrom":[makeQuery(id+"F1.opExtrude","CAP_FACE",FACE,{"disambiguationData":[OSD([sQuery(id+"F0.wireOp",EDGE,"E0"),subQ1])],"isStart":false}),makeQuery(id+"F2.opExtrude","CAP_FACE",FACE,{"disambiguationData":[OSD([subQ1,sQuery(id+"F0.wireOp",EDGE,"E4.4.0"),sQuery(id+"F0.wireOp",EDGE,"E4.4.1")])],"isStart":false}),makeQuery(id+"F2.opExtrude","CAP_FACE",FACE,{"disambiguationData":[OSD([subQ1,sQuery(id+"F0.wireOp",EDGE,"E2"),sQuery(id+"F0.wireOp",EDGE,"E3")])],"isStart":false}),makeQuery(id+"F2.opExtrude","CAP_FACE",FACE,{"disambiguationData":[OSD([subQ1,sQuery(id+"F0.wireOp",EDGE,"E4.1.0"),sQuery(id+"F0.wireOp",EDGE,"E4.1.1")])],"isStart":false}),makeQuery(id+"F2.opExtrude","CAP_FACE",FACE,{"disambiguationData":[OSD([subQ1,sQuery(id+"F0.wireOp",EDGE,"E4.2.0"),sQuery(id+"F0.wireOp",EDGE,"E4.2.1")])],"isStart":false}),makeQuery(id+"F2.opExtrude","CAP_FACE",FACE,{"disambiguationData":[OSD([subQ1,subQ0,sQuery(id+"F0.wireOp",EDGE,"E4.3.1")])],"isStart":false})]})]});}
            chamfer(context, id + "F8", {"entities" : qUnion([Q0, Q1, Q2, Q3, Q4, Q5, Q6, Q7, Q8, Q9, Q10, Q11, Q12, Q13, Q14]), "width" : 5 * mm, "tangentPropagation" : true});
        }
        {
            var Q0;
            {var subQ0=sQuery(id+"F0.wireOp",EDGE,"E1");var subQ1=makeQuery(id+"F2.opExtrude","CAP_FACE",FACE,{"disambiguationData":[OSD([subQ0,sQuery(id+"F0.wireOp",EDGE,"E4.3.0"),sQuery(id+"F0.wireOp",EDGE,"E4.3.1")])],"isStart":false});var subQ2=makeQuery(id+"F2.opExtrude","CAP_FACE",FACE,{"disambiguationData":[OSD([subQ0,sQuery(id+"F0.wireOp",EDGE,"E4.2.0"),sQuery(id+"F0.wireOp",EDGE,"E4.2.1")])],"isStart":false});var subQ3=sQuery(id+"F0.wireOp",EDGE,"E4.1.1");var subQ4=makeQuery(id+"F2.opExtrude","CAP_FACE",FACE,{"disambiguationData":[OSD([subQ0,sQuery(id+"F0.wireOp",EDGE,"E4.1.0"),subQ3])],"isStart":false});var subQ5=sQuery(id+"F0.wireOp",EDGE,"E3");var subQ6=makeQuery(id+"F2.opExtrude","CAP_FACE",FACE,{"disambiguationData":[OSD([subQ0,sQuery(id+"F0.wireOp",EDGE,"E2"),subQ5])],"isStart":false});var subQ7=makeQuery(id+"F2.opExtrude","CAP_FACE",FACE,{"disambiguationData":[OSD([subQ0,sQuery(id+"F0.wireOp",EDGE,"E4.4.0"),sQuery(id+"F0.wireOp",EDGE,"E4.4.1")])],"isStart":false});var subQ8=makeQuery(id+"F1.opExtrude","CAP_FACE",FACE,{"disambiguationData":[OSD([sQuery(id+"F0.wireOp",EDGE,"E0"),subQ0])],"isStart":false});var subQ9=makeQuery(id+"F2.boolean.opBoolean","MERGE",FACE,{"derivedFrom":[subQ8,subQ7,subQ6,subQ4,subQ2,subQ1]});Q0=makeQuery(id+"F8.opChamfer","BLEND_EDGE",EDGE,{"blendedFrom":[makeQuery(id+"F4.opChamfer","BLEND_EDGE",EDGE,{"blendedFrom":[makeQuery(id+"F2.boolean.opBoolean","SPLIT",EDGE,{"disambiguationData":[TD([makeQuery(id+"F2.opExtrude","SWEPT_FACE",FACE,{"disambiguationData":[OSD([subQ5])]})])],"derivedFrom":makeQuery(id+"F1.opExtrude","CAP_EDGE",EDGE,{"disambiguationData":[OSD([subQ0])],"isStart":false})}),subQ9],"blendedInto":[subQ9]}),subQ9],"blendedInto":[subQ9]});}
            var Q1;
            {var subQ0=sQuery(id+"F0.wireOp",EDGE,"E1");var subQ1=sQuery(id+"F0.wireOp",EDGE,"E2");var subQ2=makeQuery(id+"F2.boolean.opBoolean","MERGE",FACE,{"derivedFrom":[makeQuery(id+"F1.opExtrude","CAP_FACE",FACE,{"disambiguationData":[OSD([sQuery(id+"F0.wireOp",EDGE,"E0"),subQ0])],"isStart":false}),makeQuery(id+"F2.opExtrude","CAP_FACE",FACE,{"disambiguationData":[OSD([subQ0,sQuery(id+"F0.wireOp",EDGE,"E4.4.0"),sQuery(id+"F0.wireOp",EDGE,"E4.4.1")])],"isStart":false}),makeQuery(id+"F2.opExtrude","CAP_FACE",FACE,{"disambiguationData":[OSD([subQ0,subQ1,sQuery(id+"F0.wireOp",EDGE,"E3")])],"isStart":false}),makeQuery(id+"F2.opExtrude","CAP_FACE",FACE,{"disambiguationData":[OSD([subQ0,sQuery(id+"F0.wireOp",EDGE,"E4.1.0"),sQuery(id+"F0.wireOp",EDGE,"E4.1.1")])],"isStart":false}),makeQuery(id+"F2.opExtrude","CAP_FACE",FACE,{"disambiguationData":[OSD([subQ0,sQuery(id+"F0.wireOp",EDGE,"E4.2.0"),sQuery(id+"F0.wireOp",EDGE,"E4.2.1")])],"isStart":false}),makeQuery(id+"F2.opExtrude","CAP_FACE",FACE,{"disambiguationData":[OSD([subQ0,sQuery(id+"F0.wireOp",EDGE,"E4.3.0"),sQuery(id+"F0.wireOp",EDGE,"E4.3.1")])],"isStart":false})]});Q1=makeQuery(id+"F8.opChamfer","BLEND_EDGE",EDGE,{"blendedFrom":[makeQuery(id+"F3.opChamfer","BLEND_EDGE",EDGE,{"blendedFrom":[makeQuery(id+"F2.opExtrude","CAP_EDGE",EDGE,{"disambiguationData":[OSD([subQ1])],"isStart":false}),subQ2],"blendedInto":[subQ2]}),subQ2],"blendedInto":[subQ2]});}
            var Q2;
            {var subQ0=sQuery(id+"F0.wireOp",EDGE,"E1");var subQ1=makeQuery(id+"F2.opExtrude","CAP_FACE",FACE,{"disambiguationData":[OSD([subQ0,sQuery(id+"F0.wireOp",EDGE,"E4.3.0"),sQuery(id+"F0.wireOp",EDGE,"E4.3.1")])],"isStart":false});var subQ2=makeQuery(id+"F2.opExtrude","CAP_FACE",FACE,{"disambiguationData":[OSD([subQ0,sQuery(id+"F0.wireOp",EDGE,"E4.2.0"),sQuery(id+"F0.wireOp",EDGE,"E4.2.1")])],"isStart":false});var subQ3=makeQuery(id+"F2.opExtrude","CAP_FACE",FACE,{"disambiguationData":[OSD([subQ0,sQuery(id+"F0.wireOp",EDGE,"E4.1.0"),sQuery(id+"F0.wireOp",EDGE,"E4.1.1")])],"isStart":false});var subQ4=sQuery(id+"F0.wireOp",EDGE,"E2");var subQ5=makeQuery(id+"F2.opExtrude","CAP_FACE",FACE,{"disambiguationData":[OSD([subQ0,subQ4,sQuery(id+"F0.wireOp",EDGE,"E3")])],"isStart":false});var subQ6=sQuery(id+"F0.wireOp",EDGE,"E4.4.0");var subQ7=makeQuery(id+"F2.opExtrude","CAP_FACE",FACE,{"disambiguationData":[OSD([subQ0,subQ6,sQuery(id+"F0.wireOp",EDGE,"E4.4.1")])],"isStart":false});var subQ8=makeQuery(id+"F1.opExtrude","CAP_FACE",FACE,{"disambiguationData":[OSD([sQuery(id+"F0.wireOp",EDGE,"E0"),subQ0])],"isStart":false});var subQ9=makeQuery(id+"F2.boolean.opBoolean","MERGE",FACE,{"derivedFrom":[subQ8,subQ7,subQ5,subQ3,subQ2,subQ1]});Q2=makeQuery(id+"F8.opChamfer","BLEND_EDGE",EDGE,{"blendedFrom":[makeQuery(id+"F4.opChamfer","BLEND_EDGE",EDGE,{"blendedFrom":[makeQuery(id+"F2.boolean.opBoolean","SPLIT",EDGE,{"disambiguationData":[TD([makeQuery(id+"F2.opExtrude","SWEPT_FACE",FACE,{"disambiguationData":[OSD([subQ4])]})])],"derivedFrom":makeQuery(id+"F1.opExtrude","CAP_EDGE",EDGE,{"disambiguationData":[OSD([subQ0])],"isStart":false})}),subQ9],"blendedInto":[subQ9]}),subQ9],"blendedInto":[subQ9]});}
            var Q3;
            {var subQ0=sQuery(id+"F0.wireOp",EDGE,"E1");var subQ1=sQuery(id+"F0.wireOp",EDGE,"E4.4.1");var subQ2=makeQuery(id+"F2.boolean.opBoolean","MERGE",FACE,{"derivedFrom":[makeQuery(id+"F1.opExtrude","CAP_FACE",FACE,{"disambiguationData":[OSD([sQuery(id+"F0.wireOp",EDGE,"E0"),subQ0])],"isStart":false}),makeQuery(id+"F2.opExtrude","CAP_FACE",FACE,{"disambiguationData":[OSD([subQ0,sQuery(id+"F0.wireOp",EDGE,"E4.4.0"),subQ1])],"isStart":false}),makeQuery(id+"F2.opExtrude","CAP_FACE",FACE,{"disambiguationData":[OSD([subQ0,sQuery(id+"F0.wireOp",EDGE,"E2"),sQuery(id+"F0.wireOp",EDGE,"E3")])],"isStart":false}),makeQuery(id+"F2.opExtrude","CAP_FACE",FACE,{"disambiguationData":[OSD([subQ0,sQuery(id+"F0.wireOp",EDGE,"E4.1.0"),sQuery(id+"F0.wireOp",EDGE,"E4.1.1")])],"isStart":false}),makeQuery(id+"F2.opExtrude","CAP_FACE",FACE,{"disambiguationData":[OSD([subQ0,sQuery(id+"F0.wireOp",EDGE,"E4.2.0"),sQuery(id+"F0.wireOp",EDGE,"E4.2.1")])],"isStart":false}),makeQuery(id+"F2.opExtrude","CAP_FACE",FACE,{"disambiguationData":[OSD([subQ0,sQuery(id+"F0.wireOp",EDGE,"E4.3.0"),sQuery(id+"F0.wireOp",EDGE,"E4.3.1")])],"isStart":false})]});Q3=makeQuery(id+"F8.opChamfer","BLEND_EDGE",EDGE,{"blendedFrom":[makeQuery(id+"F3.opChamfer","BLEND_EDGE",EDGE,{"blendedFrom":[makeQuery(id+"F2.opExtrude","CAP_EDGE",EDGE,{"disambiguationData":[OSD([subQ1])],"isStart":false}),subQ2],"blendedInto":[subQ2]}),subQ2],"blendedInto":[subQ2]});}
            var Q4;
            {var subQ0=sQuery(id+"F0.wireOp",EDGE,"E4.3.0");var subQ1=sQuery(id+"F0.wireOp",EDGE,"E1");var subQ2=makeQuery(id+"F2.opExtrude","CAP_FACE",FACE,{"disambiguationData":[OSD([subQ1,subQ0,sQuery(id+"F0.wireOp",EDGE,"E4.3.1")])],"isStart":false});var subQ3=makeQuery(id+"F2.opExtrude","CAP_FACE",FACE,{"disambiguationData":[OSD([subQ1,sQuery(id+"F0.wireOp",EDGE,"E4.2.0"),sQuery(id+"F0.wireOp",EDGE,"E4.2.1")])],"isStart":false});var subQ4=makeQuery(id+"F2.opExtrude","CAP_FACE",FACE,{"disambiguationData":[OSD([subQ1,sQuery(id+"F0.wireOp",EDGE,"E4.1.0"),sQuery(id+"F0.wireOp",EDGE,"E4.1.1")])],"isStart":false});var subQ5=makeQuery(id+"F2.opExtrude","CAP_FACE",FACE,{"disambiguationData":[OSD([subQ1,sQuery(id+"F0.wireOp",EDGE,"E2"),sQuery(id+"F0.wireOp",EDGE,"E3")])],"isStart":false});var subQ6=sQuery(id+"F0.wireOp",EDGE,"E4.4.1");var subQ7=makeQuery(id+"F2.opExtrude","CAP_FACE",FACE,{"disambiguationData":[OSD([subQ1,sQuery(id+"F0.wireOp",EDGE,"E4.4.0"),subQ6])],"isStart":false});var subQ8=makeQuery(id+"F1.opExtrude","CAP_FACE",FACE,{"disambiguationData":[OSD([sQuery(id+"F0.wireOp",EDGE,"E0"),subQ1])],"isStart":false});var subQ9=makeQuery(id+"F2.boolean.opBoolean","MERGE",FACE,{"derivedFrom":[subQ8,subQ7,subQ5,subQ4,subQ3,subQ2]});Q4=makeQuery(id+"F8.opChamfer","BLEND_EDGE",EDGE,{"blendedFrom":[makeQuery(id+"F4.opChamfer","BLEND_EDGE",EDGE,{"blendedFrom":[makeQuery(id+"F2.boolean.opBoolean","SPLIT",EDGE,{"disambiguationData":[TD([makeQuery(id+"F2.opExtrude","SWEPT_FACE",FACE,{"disambiguationData":[OSD([subQ0])]})])],"derivedFrom":makeQuery(id+"F1.opExtrude","CAP_EDGE",EDGE,{"disambiguationData":[OSD([subQ1])],"isStart":false})}),subQ9],"blendedInto":[subQ9]}),subQ9],"blendedInto":[subQ9]});}
            var Q5;
            {var subQ0=sQuery(id+"F0.wireOp",EDGE,"E4.3.1");var subQ1=sQuery(id+"F0.wireOp",EDGE,"E1");var subQ2=makeQuery(id+"F2.boolean.opBoolean","MERGE",FACE,{"derivedFrom":[makeQuery(id+"F1.opExtrude","CAP_FACE",FACE,{"disambiguationData":[OSD([sQuery(id+"F0.wireOp",EDGE,"E0"),subQ1])],"isStart":false}),makeQuery(id+"F2.opExtrude","CAP_FACE",FACE,{"disambiguationData":[OSD([subQ1,sQuery(id+"F0.wireOp",EDGE,"E4.4.0"),sQuery(id+"F0.wireOp",EDGE,"E4.4.1")])],"isStart":false}),makeQuery(id+"F2.opExtrude","CAP_FACE",FACE,{"disambiguationData":[OSD([subQ1,sQuery(id+"F0.wireOp",EDGE,"E2"),sQuery(id+"F0.wireOp",EDGE,"E3")])],"isStart":false}),makeQuery(id+"F2.opExtrude","CAP_FACE",FACE,{"disambiguationData":[OSD([subQ1,sQuery(id+"F0.wireOp",EDGE,"E4.1.0"),sQuery(id+"F0.wireOp",EDGE,"E4.1.1")])],"isStart":false}),makeQuery(id+"F2.opExtrude","CAP_FACE",FACE,{"disambiguationData":[OSD([subQ1,sQuery(id+"F0.wireOp",EDGE,"E4.2.0"),sQuery(id+"F0.wireOp",EDGE,"E4.2.1")])],"isStart":false}),makeQuery(id+"F2.opExtrude","CAP_FACE",FACE,{"disambiguationData":[OSD([subQ1,sQuery(id+"F0.wireOp",EDGE,"E4.3.0"),subQ0])],"isStart":false})]});Q5=makeQuery(id+"F8.opChamfer","BLEND_EDGE",EDGE,{"blendedFrom":[makeQuery(id+"F3.opChamfer","BLEND_EDGE",EDGE,{"blendedFrom":[makeQuery(id+"F2.opExtrude","CAP_EDGE",EDGE,{"disambiguationData":[OSD([subQ0])],"isStart":false}),subQ2],"blendedInto":[subQ2]}),subQ2],"blendedInto":[subQ2]});}
            var Q6;
            {var subQ0=sQuery(id+"F0.wireOp",EDGE,"E4.3.1");var subQ1=sQuery(id+"F0.wireOp",EDGE,"E1");var subQ2=makeQuery(id+"F2.opExtrude","CAP_FACE",FACE,{"disambiguationData":[OSD([subQ1,sQuery(id+"F0.wireOp",EDGE,"E4.3.0"),subQ0])],"isStart":false});var subQ3=sQuery(id+"F0.wireOp",EDGE,"E4.2.0");var subQ4=makeQuery(id+"F2.opExtrude","CAP_FACE",FACE,{"disambiguationData":[OSD([subQ1,subQ3,sQuery(id+"F0.wireOp",EDGE,"E4.2.1")])],"isStart":false});var subQ5=makeQuery(id+"F2.opExtrude","CAP_FACE",FACE,{"disambiguationData":[OSD([subQ1,sQuery(id+"F0.wireOp",EDGE,"E4.1.0"),sQuery(id+"F0.wireOp",EDGE,"E4.1.1")])],"isStart":false});var subQ6=makeQuery(id+"F2.opExtrude","CAP_FACE",FACE,{"disambiguationData":[OSD([subQ1,sQuery(id+"F0.wireOp",EDGE,"E2"),sQuery(id+"F0.wireOp",EDGE,"E3")])],"isStart":false});var subQ7=makeQuery(id+"F2.opExtrude","CAP_FACE",FACE,{"disambiguationData":[OSD([subQ1,sQuery(id+"F0.wireOp",EDGE,"E4.4.0"),sQuery(id+"F0.wireOp",EDGE,"E4.4.1")])],"isStart":false});var subQ8=makeQuery(id+"F1.opExtrude","CAP_FACE",FACE,{"disambiguationData":[OSD([sQuery(id+"F0.wireOp",EDGE,"E0"),subQ1])],"isStart":false});var subQ9=makeQuery(id+"F2.boolean.opBoolean","MERGE",FACE,{"derivedFrom":[subQ8,subQ7,subQ6,subQ5,subQ4,subQ2]});Q6=makeQuery(id+"F8.opChamfer","BLEND_EDGE",EDGE,{"blendedFrom":[makeQuery(id+"F4.opChamfer","BLEND_EDGE",EDGE,{"blendedFrom":[makeQuery(id+"F2.boolean.opBoolean","SPLIT",EDGE,{"disambiguationData":[TD([makeQuery(id+"F2.opExtrude","SWEPT_FACE",FACE,{"disambiguationData":[OSD([subQ3])]})])],"derivedFrom":makeQuery(id+"F1.opExtrude","CAP_EDGE",EDGE,{"disambiguationData":[OSD([subQ1])],"isStart":false})}),subQ9],"blendedInto":[subQ9]}),subQ9],"blendedInto":[subQ9]});}
            var Q7;
            {var subQ0=sQuery(id+"F0.wireOp",EDGE,"E1");var subQ1=sQuery(id+"F0.wireOp",EDGE,"E4.2.1");var subQ2=makeQuery(id+"F2.boolean.opBoolean","MERGE",FACE,{"derivedFrom":[makeQuery(id+"F1.opExtrude","CAP_FACE",FACE,{"disambiguationData":[OSD([sQuery(id+"F0.wireOp",EDGE,"E0"),subQ0])],"isStart":false}),makeQuery(id+"F2.opExtrude","CAP_FACE",FACE,{"disambiguationData":[OSD([subQ0,sQuery(id+"F0.wireOp",EDGE,"E4.4.0"),sQuery(id+"F0.wireOp",EDGE,"E4.4.1")])],"isStart":false}),makeQuery(id+"F2.opExtrude","CAP_FACE",FACE,{"disambiguationData":[OSD([subQ0,sQuery(id+"F0.wireOp",EDGE,"E2"),sQuery(id+"F0.wireOp",EDGE,"E3")])],"isStart":false}),makeQuery(id+"F2.opExtrude","CAP_FACE",FACE,{"disambiguationData":[OSD([subQ0,sQuery(id+"F0.wireOp",EDGE,"E4.1.0"),sQuery(id+"F0.wireOp",EDGE,"E4.1.1")])],"isStart":false}),makeQuery(id+"F2.opExtrude","CAP_FACE",FACE,{"disambiguationData":[OSD([subQ0,sQuery(id+"F0.wireOp",EDGE,"E4.2.0"),subQ1])],"isStart":false}),makeQuery(id+"F2.opExtrude","CAP_FACE",FACE,{"disambiguationData":[OSD([subQ0,sQuery(id+"F0.wireOp",EDGE,"E4.3.0"),sQuery(id+"F0.wireOp",EDGE,"E4.3.1")])],"isStart":false})]});Q7=makeQuery(id+"F8.opChamfer","BLEND_EDGE",EDGE,{"blendedFrom":[makeQuery(id+"F3.opChamfer","BLEND_EDGE",EDGE,{"blendedFrom":[makeQuery(id+"F2.opExtrude","CAP_EDGE",EDGE,{"disambiguationData":[OSD([subQ1])],"isStart":false}),subQ2],"blendedInto":[subQ2]}),subQ2],"blendedInto":[subQ2]});}
            var Q8;
            {var subQ0=sQuery(id+"F0.wireOp",EDGE,"E1");var subQ1=makeQuery(id+"F2.opExtrude","CAP_FACE",FACE,{"disambiguationData":[OSD([subQ0,sQuery(id+"F0.wireOp",EDGE,"E4.3.0"),sQuery(id+"F0.wireOp",EDGE,"E4.3.1")])],"isStart":false});var subQ2=sQuery(id+"F0.wireOp",EDGE,"E4.2.1");var subQ3=makeQuery(id+"F2.opExtrude","CAP_FACE",FACE,{"disambiguationData":[OSD([subQ0,sQuery(id+"F0.wireOp",EDGE,"E4.2.0"),subQ2])],"isStart":false});var subQ4=sQuery(id+"F0.wireOp",EDGE,"E4.1.0");var subQ5=makeQuery(id+"F2.opExtrude","CAP_FACE",FACE,{"disambiguationData":[OSD([subQ0,subQ4,sQuery(id+"F0.wireOp",EDGE,"E4.1.1")])],"isStart":false});var subQ6=makeQuery(id+"F2.opExtrude","CAP_FACE",FACE,{"disambiguationData":[OSD([subQ0,sQuery(id+"F0.wireOp",EDGE,"E2"),sQuery(id+"F0.wireOp",EDGE,"E3")])],"isStart":false});var subQ7=makeQuery(id+"F2.opExtrude","CAP_FACE",FACE,{"disambiguationData":[OSD([subQ0,sQuery(id+"F0.wireOp",EDGE,"E4.4.0"),sQuery(id+"F0.wireOp",EDGE,"E4.4.1")])],"isStart":false});var subQ8=makeQuery(id+"F1.opExtrude","CAP_FACE",FACE,{"disambiguationData":[OSD([sQuery(id+"F0.wireOp",EDGE,"E0"),subQ0])],"isStart":false});var subQ9=makeQuery(id+"F2.boolean.opBoolean","MERGE",FACE,{"derivedFrom":[subQ8,subQ7,subQ6,subQ5,subQ3,subQ1]});Q8=makeQuery(id+"F8.opChamfer","BLEND_EDGE",EDGE,{"blendedFrom":[makeQuery(id+"F4.opChamfer","BLEND_EDGE",EDGE,{"blendedFrom":[makeQuery(id+"F2.boolean.opBoolean","SPLIT",EDGE,{"disambiguationData":[TD([makeQuery(id+"F2.opExtrude","SWEPT_FACE",FACE,{"disambiguationData":[OSD([subQ4])]})])],"derivedFrom":makeQuery(id+"F1.opExtrude","CAP_EDGE",EDGE,{"disambiguationData":[OSD([subQ0])],"isStart":false})}),subQ9],"blendedInto":[subQ9]}),subQ9],"blendedInto":[subQ9]});}
            var Q9;
            {var subQ0=sQuery(id+"F0.wireOp",EDGE,"E1");var subQ1=sQuery(id+"F0.wireOp",EDGE,"E4.1.1");var subQ2=makeQuery(id+"F2.boolean.opBoolean","MERGE",FACE,{"derivedFrom":[makeQuery(id+"F1.opExtrude","CAP_FACE",FACE,{"disambiguationData":[OSD([sQuery(id+"F0.wireOp",EDGE,"E0"),subQ0])],"isStart":false}),makeQuery(id+"F2.opExtrude","CAP_FACE",FACE,{"disambiguationData":[OSD([subQ0,sQuery(id+"F0.wireOp",EDGE,"E4.4.0"),sQuery(id+"F0.wireOp",EDGE,"E4.4.1")])],"isStart":false}),makeQuery(id+"F2.opExtrude","CAP_FACE",FACE,{"disambiguationData":[OSD([subQ0,sQuery(id+"F0.wireOp",EDGE,"E2"),sQuery(id+"F0.wireOp",EDGE,"E3")])],"isStart":false}),makeQuery(id+"F2.opExtrude","CAP_FACE",FACE,{"disambiguationData":[OSD([subQ0,sQuery(id+"F0.wireOp",EDGE,"E4.1.0"),subQ1])],"isStart":false}),makeQuery(id+"F2.opExtrude","CAP_FACE",FACE,{"disambiguationData":[OSD([subQ0,sQuery(id+"F0.wireOp",EDGE,"E4.2.0"),sQuery(id+"F0.wireOp",EDGE,"E4.2.1")])],"isStart":false}),makeQuery(id+"F2.opExtrude","CAP_FACE",FACE,{"disambiguationData":[OSD([subQ0,sQuery(id+"F0.wireOp",EDGE,"E4.3.0"),sQuery(id+"F0.wireOp",EDGE,"E4.3.1")])],"isStart":false})]});Q9=makeQuery(id+"F8.opChamfer","BLEND_EDGE",EDGE,{"blendedFrom":[makeQuery(id+"F3.opChamfer","BLEND_EDGE",EDGE,{"blendedFrom":[makeQuery(id+"F2.opExtrude","CAP_EDGE",EDGE,{"disambiguationData":[OSD([subQ1])],"isStart":false}),subQ2],"blendedInto":[subQ2]}),subQ2],"blendedInto":[subQ2]});}
            chamfer(context, id + "F9", {"entities" : qUnion([Q0, Q1, Q2, Q3, Q4, Q5, Q6, Q7, Q8, Q9]), "width" : 5 * mm, "tangentPropagation" : true});
        }
    });
